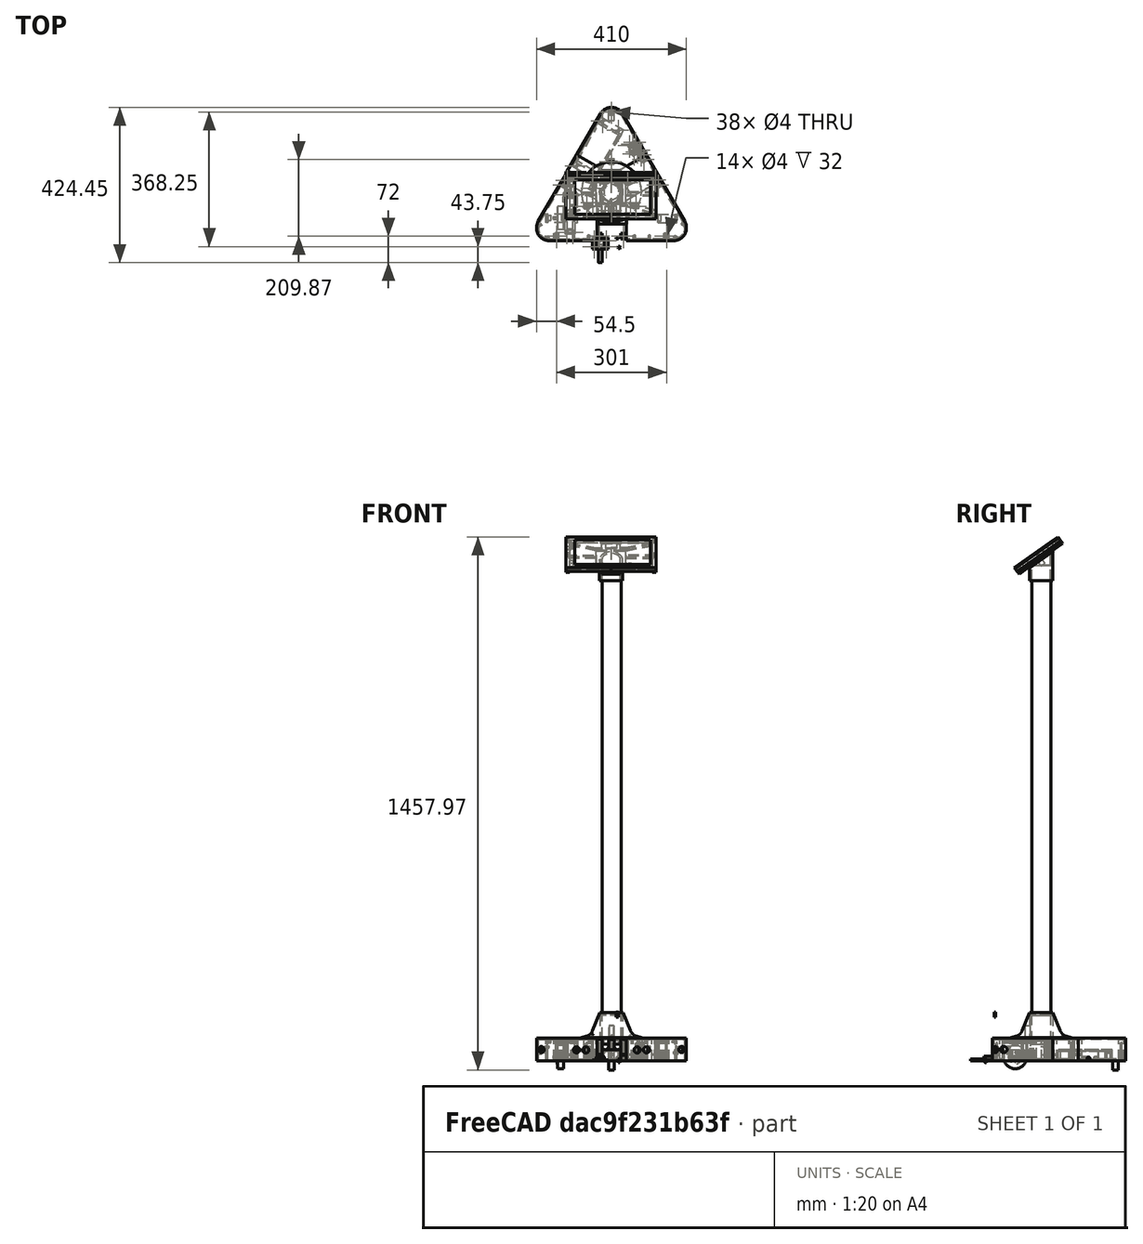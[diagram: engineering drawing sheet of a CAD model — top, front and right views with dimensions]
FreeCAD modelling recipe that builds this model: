
FCSTD DOCUMENT  (FreeCAD 0.16R6703 (Git))
Label: tabbot
License: All rights reserved
LicenseURL: http://en.wikipedia.org/wiki/All_rights_reserved
objects: Part::MultiFuse×71, Part::Cylinder×70, Part::Box×59, Part::Cut×54, Sketcher::SketchObject×18, Part::Extrusion×18, Part::Mirroring×11, App::DocumentObjectGroup×9, Part::FeaturePython×5, PartDesign::Pad×2, Part::Revolution×2, Part::Part2DObjectPython×2, Mesh::Feature×1, Image::ImagePlane×1, Part::Cone×1
note: 315 computed .brp shape members not serialized (recipe doc carries the construction recipe); baked Part::Feature solids carry a one-line shape summary decoded from their .brp

FEATURE [Part::Cylinder] Cylinder  label="Wheel"
  Angle = 360
  Height = 16
  Placement = pos=(136,62,10) rot=(0,1,0;1.5708rad)
  Radius = 31.5
FEATURE [Part::Box] Box006  label="Caster wheel"
  Height = 25
  Length = 15
  Placement = pos=(-3,329,-25) rot=(0,0,1;0rad)
  Width = 15
FEATURE [Sketcher::SketchObject] Sketch  label="Motor holder walls outline"
  sketch-geometry (17):
    g0: LineSegment StartX=20.9492 StartY=105.717 StartZ=0 EndX=5.94924 EndY=105.717 EndZ=0
    g1: LineSegment StartX=5.94924 StartY=105.717 StartZ=0 EndX=5.94924 EndY=67.2165 EndZ=0
    g2: LineSegment StartX=5.94924 StartY=67.2165 StartZ=0 EndX=78.4492 EndY=67.2165 EndZ=0
    g3: LineSegment StartX=78.4492 StartY=67.2165 StartZ=0 EndX=78.4492 EndY=73.2165 EndZ=0
    g4: LineSegment StartX=78.4492 StartY=73.2165 StartZ=0 EndX=98.4492 EndY=73.2165 EndZ=0
    g5: LineSegment StartX=98.4492 StartY=73.2165 StartZ=0 EndX=98.4492 EndY=99.7165 EndZ=0
    g6: LineSegment StartX=98.4492 StartY=99.7165 StartZ=0 EndX=93.4492 EndY=99.7165 EndZ=0
    g7: LineSegment StartX=93.4492 StartY=99.7165 StartZ=0 EndX=73.4492 EndY=99.7165 EndZ=0
    g8: LineSegment StartX=73.4492 StartY=99.7165 StartZ=0 EndX=73.4492 EndY=94.7165 EndZ=0
    g9: LineSegment StartX=73.4492 StartY=94.7165 StartZ=0 EndX=93.4492 EndY=94.7165 EndZ=0
    g10: LineSegment StartX=93.4492 StartY=94.7165 StartZ=0 EndX=93.4492 EndY=78.2165 EndZ=0
    g11: LineSegment StartX=93.4492 StartY=78.2165 StartZ=0 EndX=73.4492 EndY=78.2165 EndZ=0
    g12: LineSegment StartX=73.4492 StartY=78.2165 StartZ=0 EndX=73.4492 EndY=72.2165 EndZ=0
    g13: LineSegment StartX=73.4492 StartY=72.2165 StartZ=0 EndX=10.9492 EndY=72.2165 EndZ=0
    g14: LineSegment StartX=10.9492 StartY=72.2165 StartZ=0 EndX=10.9492 EndY=100.717 EndZ=0
    g15: LineSegment StartX=10.9492 StartY=100.717 StartZ=0 EndX=20.9492 EndY=100.717 EndZ=0
    g16: LineSegment StartX=20.9492 StartY=100.717 StartZ=0 EndX=20.9492 EndY=105.717 EndZ=0
  constraints (49):
    c: Horizontal(g0)
    c: Coincident(g0,g1)
    c: Coincident(g1,g2)
    c: Horizontal(g2)
    c: Coincident(g2,g3)
    c: Coincident(g3,g4)
    c: Horizontal(g4)
    c: Coincident(g4,g5)
    c: Vertical(g5)
    c: Coincident(g5,g6)
    c: Horizontal(g6)
    c: Coincident(g7,g8)
    c: Coincident(g8,g9)
    c: Horizontal(g9)
    c: Coincident(g9,g10)
    c: Coincident(g10,g11)
    c: Horizontal(g11)
    c: Coincident(g11,g12)
    c: Coincident(g12,g13)
    c: Horizontal(g13)
    c: Coincident(g13,g14)
    c: Coincident(g14,g15)
    c: Horizontal(g15)
    c: Coincident(g15,g16)
    c: Coincident(g16,g0)
    c: Horizontal(g7)
    c: Vertical(g10)
    c: Vertical(g12)
    c: Vertical(g14)
    c: Vertical(g1)
    c: Vertical(g16)
    c: Vertical(g3)
    c: DistanceX(g7,g7) = 20
    c: Equal(g7,g9)
    c: Vertical(g8)
    c: DistanceX(g6,g5) = 5
    c: DistanceX(g0,g14) = 5
    c: DistanceY(g15,g0) = 5
    c: DistanceX(g1,g4) = 92.5
    c: DistanceX(g0,g0) = 15
    c: DistanceY(g1,g1) = 38.5
    c: Equal(g16,g8)
    c: DistanceY(g10,g10) = 16.5
    c: DistanceY(g14,g14) = 28.5
    c: DistanceY(g2,g5) = 32.5
    c: Equal(g7,g11)
    c: Equal(g11,g4)
    c: Equal(g12,g3)
    c: Coincident(g6,g7)
FEATURE [Part::Extrusion] Extrude  label="Motor holder walls"
  Base = -> Sketch
  Dir = (0,0,49)
  Solid = true
FEATURE [PartDesign::Pad] Pad002
  Length = 3
  Length2 = 100
  Type = 0
FEATURE [Part::Cylinder] Cylinder006
  Angle = 360
  Height = 10
  Placement = pos=(1.75,3,0) rot=(0,0,1;0rad)
  Radius = 2
FEATURE [Part::MultiFuse] Fusion008  label="agujero-tornillo003"
  Placement = pos=(-8,3,5) rot=(0,1,0;3.14159rad)
  Shapes = -> [Cylinder006,Pad002]
FEATURE [Part::MultiFuse] Fusion009  label="agujero-tornillo004"
  Placement = pos=(-8,19,5) rot=(0,1,0;3.14159rad)
  Shapes = -> [Cylinder006,Pad002]
FEATURE [Part::Box] Box013  label="Screws base big"
  Height = 5
  Length = 10
  Placement = pos=(-4,67,0) rot=(0,0,1;0rad)
  Width = 38.5
FEATURE [Part::Box] Box014  label="Screws base small"
  Height = 5
  Length = 10
  Placement = pos=(98.45,73,0) rot=(0,0,1;0rad)
  Width = 26.5
FEATURE [Part::MultiFuse] Fusion011  label="Motor holder walls and wings"
  Shapes = -> [Box014,Box013,Extrude]
FEATURE [Part::MultiFuse] Fusion012  label="Screws holes small"
  Placement = pos=(113,72.5,0) rot=(0,0,1;0rad)
  Shapes = -> [Fusion009,Fusion008]
FEATURE [Part::MultiFuse] Fusion015  label="Screws holes big  "
  Placement = pos=(10.5,72.5,0) rot=(0,0,1;0rad)
FEATURE [Part::MultiFuse] Fusion016  label="Screw holes"
  Shapes = -> [Fusion012,Fusion015]
FEATURE [Sketcher::SketchObject] Sketch005  label="Motor holder ceiling outline"
  sketch-geometry (8):
    g0: LineSegment StartX=21.6465 StartY=105.635 StartZ=0 EndX=6.64649 EndY=105.635 EndZ=0
    g1: LineSegment StartX=6.64649 StartY=105.635 StartZ=0 EndX=6.64649 EndY=67.1353 EndZ=0
    g2: LineSegment StartX=6.64649 StartY=67.1353 StartZ=0 EndX=79.1465 EndY=67.1353 EndZ=0
    g3: LineSegment StartX=79.1465 StartY=67.1353 StartZ=0 EndX=79.1465 EndY=73.1353 EndZ=0
    g4: LineSegment StartX=79.1465 StartY=73.1353 StartZ=0 EndX=99.1465 EndY=73.1353 EndZ=0
    g5: LineSegment StartX=99.1465 StartY=73.1353 StartZ=0 EndX=99.1465 EndY=99.6353 EndZ=0
    g6: LineSegment StartX=99.1465 StartY=99.6353 StartZ=0 EndX=21.6465 EndY=99.6353 EndZ=0
    g7: LineSegment StartX=21.6465 StartY=99.6353 StartZ=0 EndX=21.6465 EndY=105.635 EndZ=0
  constraints (23):
    c: Horizontal(g0)
    c: Coincident(g0,g1)
    c: Coincident(g1,g2)
    c: Horizontal(g2)
    c: Coincident(g2,g3)
    c: Coincident(g3,g4)
    c: Horizontal(g4)
    c: Coincident(g4,g5)
    c: Vertical(g5)
    c: Coincident(g7,g0)
    c: Horizontal(g6)
    c: Vertical(g1)
    c: Vertical(g7)
    c: Vertical(g3)
    c: DistanceY(g7,g0) = 6
    c: DistanceX(g1,g4) = 92.5
    c: DistanceX(g0,g0) = 15
    c: DistanceY(g1,g1) = 38.5
    c: DistanceY(g2,g5) = 32.5
    c: DistanceX(g4,g4) = 20
    c: Coincident(g6,g7)
    c: DistanceY(g3,g3) = 6
    c: Coincident(g6,g5)
FEATURE [Part::Extrusion] Extrude001  label="Motor holder ceiling"
  Base = -> Sketch005
  Dir = (0,0,5)
  Placement = pos=(-0.685987,0.133377,49.0053) rot=(0,0,1;0rad)
  Solid = true
FEATURE [Part::MultiFuse] Fusion017  label="Motor holder without holes"
  Shapes = -> [Fusion011,Extrude001]
FEATURE [Part::Cylinder] Cylinder007  label="Spring hole"
  Angle = 360
  Height = 3
  Placement = pos=(52,14,-56.2) rot=(0,1,0;1.5708rad)
  Radius = 3.5
FEATURE [Part::Cylinder] Cylinder008  label="Cables hole"
  Angle = 360
  Height = 30
  Placement = pos=(3,14,-14) rot=(0,0,1;0rad)
  Radius = 5
FEATURE [Part::MultiFuse] Fusion018  label="Cable and spring holes"
  Placement = pos=(8.8,72.4,-5) rot=(0,-1,0;1.5708rad)
  Shapes = -> [Cylinder007,Cylinder008]
FEATURE [Part::MultiFuse] Fusion019  label="Holes"
  Shapes = -> [Fusion016,Fusion018]
FEATURE [Part::Cut] Cut006  label="Motor holder"
  Base = -> Fusion017
  Placement = pos=(32,126,0) rot=(0,0,-1;1.5708rad)
  Tool = -> Fusion019
FEATURE [Sketcher::SketchObject] Sketch004  label="Base Outline Bumpers"
  sketch-geometry (12):
    g0: LineSegment StartX=175 StartY=0 StartZ=0 EndX=10 EndY=0 EndZ=0
    g1: LineSegment StartX=-107.811 StartY=204.054 StartZ=0 EndX=-25.3109 EndY=346.949 EndZ=0
    g2: LineSegment StartX=35.3109 StartY=346.949 StartZ=0 EndX=117.811 EndY=204.054 EndZ=0
    g3: LineSegment StartX=-112.811 StartY=195.394 StartZ=0 EndX=-195.311 EndY=52.5 EndZ=0
    g4: LineSegment StartX=-165 StartY=0 StartZ=0 EndX=0 EndY=0 EndZ=0
    g5: LineSegment StartX=205.311 StartY=52.5 StartZ=0 EndX=122.811 EndY=195.394 EndZ=0
    g6: ArcOfCircle CenterX=-165 CenterY=35 CenterZ=0 NormalX=0 NormalY=0 NormalZ=1 Radius=35 StartAngle=2.61799 EndAngle=4.71239
    g7: ArcOfCircle CenterX=5 CenterY=329.449 CenterZ=0 NormalX=0 NormalY=0 NormalZ=1 Radius=35 StartAngle=0.523599 EndAngle=2.61799
    g8: ArcOfCircle CenterX=175 CenterY=35 CenterZ=0 NormalX=0 NormalY=0 NormalZ=1 Radius=35 StartAngle=4.71239 EndAngle=6.80678
    g9: LineSegment StartX=0 StartY=0 StartZ=0 EndX=10 EndY=0 EndZ=0
    g10: LineSegment StartX=-107.811 StartY=204.054 StartZ=0 EndX=-112.811 EndY=195.394 EndZ=0
    g11: LineSegment StartX=117.811 StartY=204.054 StartZ=0 EndX=122.811 EndY=195.394 EndZ=0
  constraints (33):
    c: Horizontal(g0)
    c: Horizontal(g4)
    c: Distance(g3,g1) = 10
    c: Parallel(g3,g1)
    c: Parallel(g2,g5)
    c: Tangent(g3,g6) = -1.5708
    c: Tangent(g4,g6) = -1.5708
    c: Tangent(g1,g7) = 1.5708
    c: Tangent(g2,g7) = 1.5708
    c: Tangent(g5,g8) = -1.5708
    c: Radius(g6) = 35
    c: Equal(g6,g7)
    c: Equal(g7,g8)
    c: Distance(g3) = 165
    c: Equal(g3,g1)
    c: Equal(g1,g2)
    c: Equal(g2,g5)
    c: Equal(g5,g0)
    c: Equal(g0,g4)
    c: Coincident(g9,g4)
    c: Coincident(g9,g0)
    c: Coincident(g0,g8)
    c: Horizontal(g9)
    c: Coincident(g10,g1)
    c: Coincident(g10,g3)
    c: Coincident(g11,g2)
    c: Coincident(g11,g5)
    c: Parallel(g10,g1)
    c: Parallel(g2,g11)
    c: Equal(g10,g11)
    c: Equal(g11,g9)
    c: Coincident(g4,g-1)
    c: Angle(g6) = 2.0944
FEATURE [Part::MultiFuse] Fusion033  label="Slider"
FEATURE [Sketcher::SketchObject] Sketch015
  Placement = pos=(0,0,0) rot=(0.57735,0.57735,0.57735;2.0944rad)
  sketch-geometry (6):
    g0: LineSegment StartX=18.75 StartY=0 StartZ=0 EndX=18.75 EndY=2 EndZ=0
    g1: LineSegment StartX=18.75 StartY=2 StartZ=0 EndX=3.75 EndY=2 EndZ=0
    g2: LineSegment StartX=18.75 StartY=0 StartZ=0 EndX=3 EndY=0 EndZ=0
    g3: LineSegment StartX=3.75 StartY=2 StartZ=0 EndX=1.5 EndY=2 EndZ=0
    g4: LineSegment StartX=1.5 StartY=2 StartZ=0 EndX=1.5 EndY=0 EndZ=0
    g5: LineSegment StartX=1.5 StartY=0 StartZ=0 EndX=3 EndY=0 EndZ=0
  constraints (18):
    c: Vertical(g0)
    c: Coincident(g0,g1)
    c: Horizontal(g1)
    c: Horizontal(g2)
    c: Coincident(g2,g0)
    c: DistanceX(g2,g2) = 15.75
    c: DistanceY(g0,g0) = 2
    c: Horizontal(g3)
    c: Coincident(g3,g4)
    c: Coincident(g4,g5)
    c: Coincident(g5,g2)
    c: Horizontal(g5)
    c: Vertical(g4)
    c: Equal(g0,g4)
    c: DistanceX(g5,g5) = 1.5
    c: DistanceX(g-1,g4) = 1.5
    c: DistanceY(g4,g-1) = 0
    c: Coincident(g3,g1)
FEATURE [Part::Revolution] Revolve
  Angle = 360
  Axis = (0,0,1)
  Base = (0,0,0)
  Solid = true
  Source = -> Sketch015
FEATURE [Sketcher::SketchObject] Sketch016
  Placement = pos=(0,0,2) rot=(0,0,1;0rad)
  sketch-geometry (3):
    g0: LineSegment StartX=-1.74642 StartY=2.8 StartZ=0 EndX=-1.74642 EndY=-2.8 EndZ=0
    g1: ArcOfCircle CenterX=0 CenterY=0 CenterZ=0 NormalX=0 NormalY=0 NormalZ=1 Radius=3.3 StartAngle=4.15471 EndAngle=8.41166
    g2: Circle CenterX=0 CenterY=0 CenterZ=0 NormalX=0 NormalY=0 NormalZ=1 Radius=4.3
  constraints (8):
    c: Vertical(g0)
    c: DistanceY(g0,g0) = 5.6
    c: Coincident(g1,g0)
    c: Coincident(g1,g0)
    c: Radius(g1) = 3.3
    c: Coincident(g2,g-1)
    c: Radius(g2) = 4.3
    c: Coincident(g1,g-1)
FEATURE [Part::Extrusion] Extrude011
  Base = -> Sketch016
  Dir = (0,0,10)
  Solid = true
FEATURE [Part::Extrusion] Extrude012  label="Base"
  Base = -> Sketch004
  Dir = (0,0,-5)
  Solid = true
FEATURE [Part::MultiFuse] Fusion039  label="Encoder piece"
  Placement = pos=(175,47,10) rot=(0,1,0;1.5708rad)
  Shapes = -> [Revolve,Extrude011]
FEATURE [Mesh::Feature] User_Library_HC_SR005  label="User Library-HC-SR005"
  Placement = pos=(-141.804,49.5,15) rot=(0.774597,-0.447214,-0.447214;1.82349rad)
FEATURE [App::DocumentObjectGroup] Group  label="Trial"
FEATURE [Part::Box] Box023  label="Battery001"
  Height = 26
  Length = 115
  Width = 60
FEATURE [Part::Box] Box024  label="Board001"
  Height = 30
  Length = 80
  Placement = pos=(-31,45,0) rot=(0,0,1;0rad)
  Width = 55
FEATURE [Part::Box] Box025  label="Switch001"
  Height = 22
  Length = 12
  Placement = pos=(0,-40,0) rot=(0,0,1;0rad)
  Width = 40
FEATURE [Part::MultiFuse] Fusion045  label="Battery + switch001"
  Placement = pos=(-29.9027,319.105,0) rot=(0,0,-1;2.0944rad)
  Shapes = -> [Box025,Box023]
FEATURE [PartDesign::Pad] Pad003
  Length = 20
  Length2 = 100
  Type = 0
FEATURE [Part::Cylinder] Cylinder013
  Angle = 360
  Height = 10
  Placement = pos=(1.75,3,0) rot=(0,0,1;0rad)
  Radius = 2
FEATURE [Sketcher::SketchObject] Sketch028  label="Battery holder walls outline001"
  sketch-geometry (10):
    g0: LineSegment StartX=19.4089 StartY=-79.555 StartZ=0 EndX=19.4089 EndY=-7.55496 EndZ=0
    g1: LineSegment StartX=19.4089 StartY=-7.55496 StartZ=0 EndX=-108.591 EndY=-7.55496 EndZ=0
    g2: LineSegment StartX=-108.591 StartY=-7.55496 StartZ=0 EndX=-108.591 EndY=-79.555 EndZ=0
    g3: LineSegment StartX=-108.591 StartY=-79.555 StartZ=0 EndX=-103.591 EndY=-79.555 EndZ=0
    g4: LineSegment StartX=-103.591 StartY=-79.555 StartZ=0 EndX=-103.591 EndY=-12.555 EndZ=0
    g5: LineSegment StartX=-103.591 StartY=-12.555 StartZ=0 EndX=14.4089 EndY=-12.555 EndZ=0
    g6: LineSegment StartX=14.4089 StartY=-12.555 StartZ=0 EndX=14.4089 EndY=-74.555 EndZ=0
    g7: LineSegment StartX=14.4089 StartY=-74.555 StartZ=0 EndX=-90.5911 EndY=-74.555 EndZ=0
    g8: LineSegment StartX=-90.5911 StartY=-74.555 StartZ=0 EndX=-90.5911 EndY=-79.555 EndZ=0
    g9: LineSegment StartX=-90.5911 StartY=-79.555 StartZ=0 EndX=19.4089 EndY=-79.555 EndZ=0
  constraints (28):
    c: Vertical(g0)
    c: Coincident(g0,g1)
    c: Horizontal(g1)
    c: Coincident(g1,g2)
    c: Vertical(g2)
    c: Coincident(g2,g3)
    c: Coincident(g3,g4)
    c: Vertical(g4)
    c: Coincident(g4,g5)
    c: Horizontal(g5)
    c: Coincident(g5,g6)
    c: Vertical(g6)
    c: Coincident(g6,g7)
    c: Horizontal(g7)
    c: Coincident(g7,g8)
    c: Vertical(g8)
    c: Coincident(g8,g9)
    c: Coincident(g9,g0)
    c: Horizontal(g9)
    c: Horizontal(g3)
    c: Equal(g2,g0)
    c: DistanceX(g3,g3) = 5
    c: DistanceY(g8,g8) = 5
    c: DistanceY(g5,g0) = 5
    c: DistanceX(g6,g0) = 5
    c: DistanceX(g5,g5) = 118
    c: DistanceX(g7,g7) = 105
    c: DistanceY(g6,g6) = 62
FEATURE [Part::Extrusion] Extrude022  label="Battery holder walls001"
  Base = -> Sketch028
  Dir = (0,0,26)
  Solid = true
FEATURE [Part::MultiFuse] Fusion046  label="battery screw 005"
  Placement = pos=(-113,-22,5) rot=(0,1,0;3.14159rad)
  Shapes = -> [Cylinder013,Pad003]
FEATURE [Part::Cylinder] Cylinder014  label="Battery cables hole001"
  Angle = 360
  Height = 20
  Placement = pos=(-98,0,8.5) rot=(1,0,0;1.5708rad)
  Radius = 4.5
FEATURE [Part::Box] Box027  label="Screw plane 003"
  Height = 5
  Length = 15
  Placement = pos=(18.5,-79.5,0) rot=(0,0,1;0rad)
  Width = 72
FEATURE [Part::Box] Box028  label="Screw plane 004"
  Height = 5
  Length = 15
  Placement = pos=(-122.5,-79.5,0) rot=(0,0,1;0rad)
  Width = 72
FEATURE [Part::MultiFuse] Fusion048  label="battery screw 006"
  Placement = pos=(-113,-72,5) rot=(0,1,0;3.14159rad)
  Shapes = -> [Cylinder013,Pad003]
FEATURE [Part::MultiFuse] Fusion049  label="battery screw 007"
  Placement = pos=(28,-72,5) rot=(0,1,0;3.14159rad)
  Shapes = -> [Cylinder013,Pad003]
FEATURE [Part::MultiFuse] Fusion050  label="battery screw 008"
  Placement = pos=(28,-22,5) rot=(0,1,0;3.14159rad)
  Shapes = -> [Cylinder013,Pad003]
FEATURE [Part::MultiFuse] Fusion051  label="Battery screws001"
  Shapes = -> [Fusion046,Fusion048,Fusion049,Fusion050]
FEATURE [Part::MultiFuse] Fusion052  label="Battery holes001"
  Shapes = -> [Fusion051,Cylinder014]
FEATURE [App::DocumentObjectGroup] Group005  label="Future"
  Group = -> [Fusion033]
FEATURE [Part::FeaturePython] Point  label="Center base"  # WARN: FeaturePython — macro-defined, semantics opaque (R4)
  X = 5
  Y = 133.15
  Z = 0
FEATURE [Sketcher::SketchObject] Sketch030  label="US sensor holes 001"
  Placement = pos=(0,0,0) rot=(1,0,0;1.5708rad)
  sketch-geometry (2):
    g0: Circle CenterX=-50.6795 CenterY=14.9384 CenterZ=0 NormalX=0 NormalY=0 NormalZ=1 Radius=8.5
    g1: Circle CenterX=-25.1765 CenterY=14.826 CenterZ=0 NormalX=0 NormalY=0 NormalZ=1 Radius=8.5
  constraints (2):
    c: Radius(g0) = 8.5
    c: Equal(g0,g1) = 9
FEATURE [Part::Extrusion] Extrude027  label="US holes003"
  Base = -> Sketch030
  Dir = (0,50,0)
  Placement = pos=(0,-11,15) rot=(0,0,1;0rad)
  Solid = true
FEATURE [Part::Extrusion] Extrude028  label="US holes004"
  Base = -> Sketch030
  Dir = (0,50,0)
  Placement = pos=(-145,-20,16) rot=(0,0,-1;1.0472rad)
  Solid = true
FEATURE [Sketcher::SketchObject] Sketch031  label="US sensor holes screws001"
  Placement = pos=(0,0,0) rot=(1,0,0;1.5708rad)
  sketch-geometry (2):
    g0: Circle CenterX=-57.9482 CenterY=6.7605 CenterZ=0 NormalX=0 NormalY=0 NormalZ=1 Radius=1.4
    g1: Circle CenterX=-17.0367 CenterY=23.1516 CenterZ=0 NormalX=0 NormalY=0 NormalZ=1 Radius=1.4
  constraints (2):
    c: Radius(g0) = 1.4
    c: Equal(g0,g1) = 1.4
FEATURE [Part::Extrusion] Extrude029  label="US sensor holes screws extruded001"
  Base = -> Sketch031
  Dir = (0,30,0)
  Placement = pos=(0,5,15) rot=(0,0,1;0rad)
  Solid = true
FEATURE [Part::MultiFuse] Fusion057  label="US holes005"
  Placement = pos=(-40,0,0) rot=(0,0,1;0rad)
  Shapes = -> [Extrude027,Extrude028]
FEATURE [Part::Box] Box029  label="Wall 003"
  Height = 58
  Length = 130
  Placement = pos=(-125,0,0) rot=(0,0,1;0rad)
  Width = 5
FEATURE [Part::Cylinder] Cylinder015  label="Curve out001"
  Angle = 120
  Height = 58
  Placement = pos=(-100,35,0) rot=(0,0,1;2.61799rad)
  Radius = 35
FEATURE [Part::Box] Box030  label="Wall 004"
  Height = 58
  Length = 130
  Placement = pos=(-150.981,50,0) rot=(0,0,1;1.0472rad)
  Width = 5
FEATURE [Part::Cylinder] Cylinder016  label="Curve in001"
  Angle = 120
  Height = 58
  Placement = pos=(-100,35,0) rot=(0,0,1;2.61799rad)
  Radius = 30
FEATURE [Part::Cut] Cut020  label="Curve001"
  Base = -> Cylinder015
  Placement = pos=(-25,0,0) rot=(0,0,1;0rad)
  Tool = -> Cylinder016
FEATURE [Part::Box] Box031  label="Top 002"
  Height = 4
  Length = 130
  Placement = pos=(-125,0,58) rot=(0,0,1;0rad)
  Width = 35
FEATURE [Part::Cylinder] Cylinder017  label="Top curve001"
  Angle = 120
  Height = 4
  Placement = pos=(-125,35,58) rot=(0,0,1;2.61799rad)
  Radius = 35
FEATURE [Part::MultiFuse] Fusion058  label="Bumper walls"
  Placement = pos=(-40,0,0) rot=(0,0,1;0rad)
  Shapes = -> [Box029,Box030,Cut020]
FEATURE [Part::Box] Box032  label="Support 004"
  Height = 6
  Length = 6
  Placement = pos=(-20,5,35) rot=(0,0,1;0rad)
  Width = 10
FEATURE [Part::Box] Box033  label="Support 005"
  Height = 6
  Length = 6
  Placement = pos=(-61,5,19) rot=(0,0,1;0rad)
  Width = 10
FEATURE [Part::MultiFuse] Fusion059  label="Support 006"
  Shapes = -> [Box032,Box033]
FEATURE [Part::Cut] Cut024  label="US support003"
  Base = -> Fusion059
  Placement = pos=(-40,0,0) rot=(0,0,1;0rad)
  Tool = -> Extrude029
FEATURE [Part::Cut] Cut025  label="US support004"
  Base = -> Fusion059
  Placement = pos=(-171,-13,0) rot=(0,0,-1;1.0472rad)
  Tool = -> Extrude029
FEATURE [Part::Box] Box034  label="Top 003"
  Height = 4
  Length = 130
  Placement = pos=(-90.3109,165.083,58) rot=(0,0,-1;2.0944rad)
  Width = 35
FEATURE [Part::MultiFuse] Fusion066  label="Bumper walls001"
  Placement = pos=(-87.811,238.695,0) rot=(0,0,-1;2.0944rad)
  Shapes = -> [Box029,Box030,Cut020]
FEATURE [Part::Box] Box  label="Cube"
  Height = 58
  Length = 15
  Placement = pos=(-13,5,0) rot=(0,0,1;0rad)
  Width = 15
FEATURE [Part::Cylinder] Cylinder018  label="Cylinder"
  Angle = 360
  Height = 50
  Placement = pos=(-5.5,12,0) rot=(0,0,1;0rad)
  Radius = 2
FEATURE [Part::Cut] Cut  label="Bumper support 001"
  Base = -> Box
  Tool = -> Cylinder018
FEATURE [Part::Box] Box035  label="Nut hole"
  Height = 3
  Length = 6
  Placement = pos=(-8.5,5,15) rot=(0,0,1;0rad)
  Width = 15
FEATURE [Part::Cut] Cut031  label="Bumper support 005"
  Base = -> Cut
  Placement = pos=(-140,0,0) rot=(0,0,1;0rad)
  Tool = -> Box035
FEATURE [Part::Cut] Cut032  label="Bumper support 006"
  Base = -> Cut
  Placement = pos=(-136.811,153.825,0) rot=(0,0,-1;2.0944rad)
  Tool = -> Box035
FEATURE [Sketcher::SketchObject] Sketch032
  Placement = pos=(0,0,0) rot=(1,0,0;1.5708rad)
  sketch-geometry (7):
    g0: LineSegment StartX=12.1868 StartY=134.984 StartZ=0 EndX=32.1868 EndY=134.984 EndZ=0
    g1: LineSegment StartX=32.1868 StartY=134.984 StartZ=0 EndX=52.1868 EndY=84.9837 EndZ=0
    g2: LineSegment StartX=69.6638 StartY=69.9351 StartZ=0 EndX=82.1868 EndY=66.9837 EndZ=0
    g3: LineSegment StartX=82.1868 StartY=66.9837 StartZ=0 EndX=82.1868 EndY=64.9837 EndZ=0
    g4: LineSegment StartX=82.1868 StartY=64.9837 StartZ=0 EndX=12.1868 EndY=64.9837 EndZ=0
    g5: ArcOfCircle CenterX=75.3987 CenterY=94.2684 CenterZ=0 NormalX=0 NormalY=0 NormalZ=1 Radius=25 StartAngle=3.5221 EndAngle=4.48093
    g6: LineSegment StartX=12.1868 StartY=64.9837 StartZ=0 EndX=12.1868 EndY=134.984 EndZ=0
  constraints (18):
    c: Horizontal(g0)
    c: Coincident(g0,g1)
    c: Coincident(g2,g3)
    c: Coincident(g3,g4)
    c: Horizontal(g4)
    c: Vertical(g3)
    c: DistanceY(g3,g3) = 2
    c: Tangent(g1,g5) = -1.5708
    c: Tangent(g2,g5) = -1.5708
    c: DistanceX(g0,g0) = 20
    c: DistanceY(g3,g0) = 70
    c: DistanceX(g0,g2) = 50
    c: DistanceY(g1,g1) = 50
    c: DistanceX(g1,g1) = 20
    c: Coincident(g4,g6)
    c: Coincident(g6,g0)
    c: Vertical(g6)
    c: Radius(g5) = 25
FEATURE [Part::Revolution] Revolve001  label="Embellecedor"
  Angle = 360
  Axis = (0,0,1)
  Base = (0,0,0)
  Placement = pos=(5,133,0) rot=(0,0,1;0rad)
  Solid = true
  Source = -> Sketch032
FEATURE [Part::MultiFuse] Fusion075  label="Tubes"
FEATURE [Part::Part2DObjectPython] DWire  # Draft 2D object (typed FeaturePython)
  ChamferSize = 0
  Closed = true
  End = (5,110.056,62)
  FilletRadius = 0
  Length = 410.111
  MakeFace = true
  Points = (4) [(-60,147.583,62),(-125,35,62),(5,35,62),(5,110.056,62)]
  Start = (-60,147.583,62)
  Subdivisions = 0
FEATURE [Part::Extrusion] Extrude030
  Base = -> DWire
  Dir = (0,0,-4)
  Solid = true
FEATURE [Part::MultiFuse] Fusion076  label="Bumper top"
  Placement = pos=(-40,0,0) rot=(0,0,1;0rad)
  Shapes = -> [Cylinder017,Box034,Box031,Extrude030]
FEATURE [Part::Box] Box038  label="Cube002"
  Height = 58
  Length = 80
  Placement = pos=(-35,0,0) rot=(0,0,1;0rad)
  Width = 5
FEATURE [Part::Box] Box039  label="Cube003"
  Height = 4
  Length = 80
  Placement = pos=(-35,0,58) rot=(0,0,1;0rad)
  Width = 90
FEATURE [Part::MultiFuse] Fusion081  label="Extension 001"
  Shapes = -> [Box039,Box038]
FEATURE [Part::Cut] Cut037  label="Bumper support 011"
  Base = -> Cut
  Placement = pos=(-22,0,0) rot=(0,0,1;0rad)
  Tool = -> Box035
FEATURE [Part::Cut] Cut038  label="Bumper support 012"
  Base = -> Cut
  Placement = pos=(43,0,0) rot=(0,0,1;0rad)
  Tool = -> Box035
FEATURE [Part::Cut] Cut039  label="Bumper support 013"
  Base = -> Cut
  Placement = pos=(10,70,0) rot=(0,0,1;0rad)
  Tool = -> Box035
FEATURE [Part::MultiFuse] Fusion082  label="Extension supports"
  Shapes = -> [Cut039,Cut037,Cut038]
FEATURE [Part::MultiFuse] Fusion083  label="M3 screw"
  Placement = pos=(28,-22,5) rot=(0,1,0;3.14159rad)
  Shapes = -> [Cylinder013,Pad003]
FEATURE [Part::Cylinder] Cylinder021  label="M3 hole"
  Angle = 360
  Height = 15
  Placement = pos=(-46.5,104,58) rot=(0,0,1;0rad)
  Radius = 2
FEATURE [Part::Cylinder] Cylinder022  label="M3 hole001"
  Angle = 360
  Height = 15
  Placement = pos=(-46.5,104,58) rot=(0,0,1;0rad)
  Radius = 2
FEATURE [Part::Cut] Cut041  label="Bumper top with hole"
  Base = -> Fusion076
  Tool = -> Cylinder021
FEATURE [Part::MultiFuse] Fusion084  label="Extension with supports 001"
  Shapes = -> [Fusion081,Fusion082]
FEATURE [Part::FeaturePython] Clone002  label="Extension with supports 002"  # Draft clone (typed FeaturePython)
  Objects = -> [Fusion084]
  Placement = pos=(122.811,195.394,0) rot=(0,0,1;2.0944rad)
  Scale = (1,1,1)
FEATURE [Part::FeaturePython] Clone004  label="Clone of Bumper top with hole"  # Draft clone (typed FeaturePython)
  Objects = -> [Cut041]
  Placement = pos=(-107.811,204.054,0) rot=(0,0,-1;2.0944rad)
  Scale = (1,1,1)
FEATURE [Part::Cut] Cut042  label="Bumper support 014"
  Base = -> Cut
  Placement = pos=(-57,82,0) rot=(0,0,1;0rad)
  Tool = -> Box035
FEATURE [Part::MultiFuse] Fusion085  label="Bumper supports"
  Shapes = -> [Cut031,Cut042,Cut032]
FEATURE [Part::Box] Box040  label="Cube004"
  Height = 58
  Length = 15
  Placement = pos=(-13,5,0) rot=(0,0,1;0rad)
  Width = 15
FEATURE [Part::Cylinder] Cylinder023  label="Cylinder015"
  Angle = 360
  Height = 50
  Placement = pos=(-5.5,12,0) rot=(0,0,1;0rad)
  Radius = 2
FEATURE [Part::Cut] Cut043  label="Bumper support 015"
  Base = -> Box040
  Tool = -> Cylinder023
FEATURE [Part::Box] Box041  label="Nut hole001"
  Height = 4
  Length = 8
  Placement = pos=(-9.5,5,15) rot=(0,0,1;0rad)
  Width = 15
FEATURE [Part::Cut] Cut044  label="Bumper support 016"
  Base = -> Cut043
  Placement = pos=(10,340,0) rot=(0,0,1;0rad)
  Tool = -> Box041
FEATURE [Part::Cut] Cut045  label="Bumper support 017"
  Base = -> Cut043
  Placement = pos=(10,204,0) rot=(0,0,1;0rad)
  Tool = -> Box041
FEATURE [Part::Cut] Cut046  label="Bumper support 018"
  Base = -> Cut043
  Placement = pos=(93.7959,245.482,0) rot=(0,0,1;2.0944rad)
  Tool = -> Box041
FEATURE [Part::MultiFuse] Fusion088  label="Supports bumper back "
  Shapes = -> [Cut044,Cut046,Cut045]
FEATURE [Part::MultiFuse] Fusion089  label="Bumper back"
  Shapes = -> [Clone004,Fusion066,Fusion088]
FEATURE [Part::Box] Box042  label="Cube005"
  Height = 58
  Length = 15
  Placement = pos=(-13,5,0) rot=(0,0,1;0rad)
  Width = 15
FEATURE [Part::Cylinder] Cylinder024  label="Cylinder016"
  Angle = 360
  Height = 50
  Placement = pos=(-5.5,12,0) rot=(0,0,1;0rad)
  Radius = 2
FEATURE [Part::Cut] Cut047  label="Bumper support 019"
  Base = -> Box042
  Tool = -> Cylinder024
FEATURE [Part::Box] Box043  label="Nut hole002"
  Height = 3
  Length = 6
  Placement = pos=(-8.5,5,15) rot=(0,0,1;0rad)
  Width = 15
FEATURE [Part::Box] Box044  label="Cube006"
  Height = 58
  Length = 80
  Placement = pos=(-35,0,0) rot=(0,0,1;0rad)
  Width = 5
FEATURE [Part::Box] Box045  label="Cube007"
  Height = 4
  Length = 80
  Placement = pos=(-35,0,58) rot=(0,0,1;0rad)
  Width = 90
FEATURE [Part::MultiFuse] Fusion090  label="Extension 002"
  Placement = pos=(-107.811,204.054,0) rot=(0,0,-1;2.0944rad)
  Shapes = -> [Box045,Box044]
FEATURE [Part::Cut] Cut049  label="Bumper support 021"
  Base = -> Cut047
  Placement = pos=(43,0,0) rot=(0,0,1;0rad)
  Tool = -> Box043
FEATURE [Part::Cut] Cut050  label="Bumper support 022"
  Base = -> Cut047
  Placement = pos=(10,70,0) rot=(0,0,1;0rad)
  Tool = -> Box043
FEATURE [Part::Cut] Cut048  label="Bumper support 020"
  Base = -> Cut047
  Placement = pos=(-22,0,0) rot=(0,0,1;0rad)
  Tool = -> Box043
FEATURE [Part::MultiFuse] Fusion091  label="Extension supports001"
  Shapes = -> [Cut050,Cut048,Cut049]
FEATURE [Part::Cut] Cut051  label="Bumper support 023"
  Base = -> Cut
  Placement = pos=(-102.16,163.842,0) rot=(0,0,1;1.0472rad)
  Tool = -> Box035
FEATURE [Part::Cut] Cut052  label="Bumper support 024"
  Base = -> Cut
  Placement = pos=(-33.7717,142.497,0) rot=(0,0,1;1.0472rad)
  Tool = -> Box035
FEATURE [Part::MultiFuse] Fusion092  label="Extension with supports 003"
  Shapes = -> [Fusion090,Cut051,Cut052]
FEATURE [App::DocumentObjectGroup] Group006  label="Extensions"
  Group = -> [Fusion084,Clone002,Fusion092]
FEATURE [Part::Cylinder] Cylinder025  label="M3 hole002"
  Angle = 360
  Height = 15
  Placement = pos=(-46.5,104,58) rot=(0,0,1;0rad)
  Radius = 2
FEATURE [Part::Cylinder] Cylinder026  label="M3 hole003"
  Angle = 360
  Height = 15
  Placement = pos=(56.5,104,58) rot=(0,0,1;0rad)
  Radius = 2
FEATURE [Part::Cylinder] Cylinder027  label="M3 hole004"
  Angle = 360
  Height = 15
  Placement = pos=(5.5,192.5,58) rot=(0,0,1;0rad)
  Radius = 2
FEATURE [Part::Box] Box046  label="Cube008"
  Height = 5
  Length = 52
  Placement = pos=(154.769,38,49.0053) rot=(0,0,1;0rad)
  Width = 23
FEATURE [Part::Box] Box047  label="Cube009"
  Height = 49
  Length = 5
  Placement = pos=(201.769,38,0.00526065) rot=(0,0,1;0rad)
  Width = 23
FEATURE [Part::MultiFuse] Fusion094  label="Encoder support"
  Placement = pos=(0,-4,0) rot=(0,0,1;0rad)
  Shapes = -> [Box046,Box047]
FEATURE [Part::Box] Box048  label="Cube010"
  Height = 40
  Length = 2
  Placement = pos=(203.5,37,2) rot=(0,0,1;0rad)
  Width = 19
FEATURE [Part::Cylinder] Cylinder030  label="M3 hole007"
  Angle = 360
  Height = 15
  Placement = pos=(163.5,47,22.5) rot=(0,1,0;1.5708rad)
  Radius = 1.5
FEATURE [Part::Cylinder] Cylinder031  label="M3 hole008"
  Angle = 360
  Height = 15
  Placement = pos=(163.5,47,-2.5) rot=(0,1,0;1.5708rad)
  Radius = 1.5
FEATURE [Part::MultiFuse] Fusion096  label="Encoder-to-wheel holes"
  Shapes = -> [Cylinder030,Cylinder031]
FEATURE [Part::Cut] Cut055  label="Encoder-to-wheel piece"
  Base = -> Fusion039
  Placement = pos=(-23,15,0) rot=(0,0,1;0rad)
  Tool = -> Fusion096
FEATURE [Part::MultiFuse] Fusion  label="Battery support without holes"
  Shapes = -> [Extrude022,Box027,Box028]
FEATURE [Part::Cut] Cut056  label="Battery support without ceiling"
  Base = -> Fusion
  Placement = pos=(-16.6317,192.981,0) rot=(0,0,-1;2.0944rad)
  Tool = -> Fusion052
FEATURE [Part::Box] Box049  label="Battery support top"
  Height = 5
  Length = 128
  Placement = pos=(-31.2328,326.801,26) rot=(0,0,-1;2.0944rad)
  Width = 72
FEATURE [Part::MultiFuse] Fusion097  label="Battery support"
  Shapes = -> [Cut056,Box049]
FEATURE [Part::Cut] Cut040  label="Trim with pipe hole"
  Base = -> Revolve001
  Tool = -> Fusion075
FEATURE [Part::MultiFuse] Fusion098  label="Trim holes"
  Shapes = -> [Cylinder025,Cylinder026,Cylinder027]
FEATURE [Part::Cut] Cut057  label="Trim with support holes"
  Base = -> Cut040
  Tool = -> Fusion098
FEATURE [Part::Box] Box050  label="Cube011"
  Height = 50
  Length = 13
  Placement = pos=(-1.5,90,50) rot=(0,0,1;0.017453rad)
  Width = 13
FEATURE [Part::Cut] Cut058  label="Trim complete"
  Base = -> Cut057
  Placement = pos=(0,0,-3) rot=(0,0,1;0rad)
  Tool = -> Box050
FEATURE [Sketcher::SketchObject] Sketch033
  Placement = pos=(0,0,0) rot=(1,0,0;1.5708rad)
  sketch-geometry (31):
    g0: LineSegment StartX=-81.8917 StartY=135.847 StartZ=0 EndX=-71.8917 EndY=135.847 EndZ=0
    g1: LineSegment StartX=-71.8917 StartY=135.847 StartZ=0 EndX=-71.8917 EndY=125.847 EndZ=0
    g2: LineSegment StartX=-71.8917 StartY=125.847 StartZ=0 EndX=0.608279 EndY=103.681 EndZ=0
    g3: LineSegment StartX=40.6083 StartY=103.681 StartZ=0 EndX=40.6083 EndY=22.012 EndZ=0
    g4: LineSegment StartX=0.608279 StartY=22.012 StartZ=0 EndX=-71.8917 EndY=-0.153498 EndZ=0
    g5: LineSegment StartX=-71.8917 StartY=-0.153498 StartZ=0 EndX=-71.8917 EndY=-10.1535 EndZ=0
    g6: LineSegment StartX=-71.8917 StartY=-10.1535 StartZ=0 EndX=-81.8917 EndY=-10.1535 EndZ=0
    g7: LineSegment StartX=-81.8917 StartY=-10.1535 StartZ=0 EndX=-81.8917 EndY=6.7892 EndZ=0
    g8: LineSegment StartX=-81.8917 StartY=6.7892 StartZ=0 EndX=0.608279 EndY=32.012 EndZ=0
    g9: LineSegment StartX=0.608279 StartY=32.012 StartZ=0 EndX=0.608279 EndY=57.8465 EndZ=0
    g10: LineSegment StartX=0.608279 StartY=57.8465 StartZ=0 EndX=-81.8917 EndY=57.8465 EndZ=0
    g11: LineSegment StartX=-81.8917 StartY=57.8465 StartZ=0 EndX=-81.8917 EndY=67.8465 EndZ=0
    g12: LineSegment StartX=-81.8917 StartY=67.8465 StartZ=0 EndX=0.608279 EndY=67.8465 EndZ=0
    g13: LineSegment StartX=0.608279 StartY=67.8465 StartZ=0 EndX=0.608279 EndY=93.681 EndZ=0
    g14: LineSegment StartX=0.608279 StartY=93.681 StartZ=0 EndX=-81.8917 EndY=118.904 EndZ=0
    g15: LineSegment StartX=-81.8917 StartY=118.904 StartZ=0 EndX=-81.8917 EndY=135.847 EndZ=0
    g16: Circle CenterX=-76.8917 CenterY=130.847 CenterZ=0 NormalX=0 NormalY=0 NormalZ=1 Radius=2
    g17: Circle CenterX=-76.8917 CenterY=62.8465 CenterZ=0 NormalX=0 NormalY=0 NormalZ=1 Radius=2
    g18: Circle CenterX=-76.8917 CenterY=-5.1535 CenterZ=0 NormalX=0 NormalY=0 NormalZ=1 Radius=2
    g19: LineSegment StartX=0.608279 StartY=103.681 StartZ=0 EndX=15.6083 EndY=103.681 EndZ=0
    g20: LineSegment StartX=15.6083 StartY=103.681 StartZ=0 EndX=15.6083 EndY=135.681 EndZ=0
    g21: LineSegment StartX=15.6083 StartY=135.681 StartZ=0 EndX=25.6083 EndY=135.681 EndZ=0
    g22: LineSegment StartX=25.6083 StartY=135.681 StartZ=0 EndX=25.6083 EndY=103.681 EndZ=0
    g23: LineSegment StartX=25.6083 StartY=103.681 StartZ=0 EndX=40.6083 EndY=103.681 EndZ=0
    g24: LineSegment StartX=0.608279 StartY=22.012 StartZ=0 EndX=15.6083 EndY=22.012 EndZ=0
    g25: LineSegment StartX=15.6083 StartY=22.012 StartZ=0 EndX=15.6083 EndY=-9.98802 EndZ=0
    g26: LineSegment StartX=15.6083 StartY=-9.98802 StartZ=0 EndX=25.6083 EndY=-9.98802 EndZ=0
    g27: LineSegment StartX=25.6083 StartY=-9.98802 StartZ=0 EndX=25.6083 EndY=22.012 EndZ=0
    g28: LineSegment StartX=25.6083 StartY=22.012 StartZ=0 EndX=40.6083 EndY=22.012 EndZ=0
    g29: Circle CenterX=20.6083 CenterY=130.681 CenterZ=0 NormalX=0 NormalY=0 NormalZ=1 Radius=2
    g30: Circle CenterX=20.6083 CenterY=-4.98802 CenterZ=0 NormalX=0 NormalY=0 NormalZ=1 Radius=2
  constraints (91):
    c: Horizontal(g0)
    c: Coincident(g0,g1)
    c: Vertical(g1)
    c: Coincident(g1,g2)
    c: Vertical(g3)
    c: Coincident(g4,g5)
    c: Vertical(g5)
    c: Coincident(g5,g6)
    c: Horizontal(g6)
    c: Coincident(g6,g7)
    c: Vertical(g7)
    c: Coincident(g7,g8)
    c: Coincident(g8,g9)
    c: Vertical(g9)
    c: Coincident(g9,g10)
    c: Horizontal(g10)
    c: Coincident(g10,g11)
    c: Coincident(g11,g12)
    c: Horizontal(g12)
    c: Coincident(g12,g13)
    c: Coincident(g13,g14)
    c: Coincident(g14,g15)
    c: Coincident(g15,g0)
    c: Vertical(g13)
    c: Vertical(g11)
    c: Radius(g16) = 2
    c: DistanceX(g0,g16) = 5
    c: DistanceY(g16,g0) = 5
    c: Vertical(g15)
    c: DistanceX(g0,g0) = 10
    c: DistanceX(g1,g3) = 112.5
    c: Equal(g16,g17)
    c: Equal(g17,g18)
    c: Parallel(g14,g2)
    c: Parallel(g4,g8)
    c: DistanceX(g6,g18) = 5
    c: DistanceY(g6,g18) = 5
    c: DistanceX(g6,g6) = 10
    c: DistanceY(g5,g5) = 10
    c: DistanceY(g1,g1) = 10
    c: DistanceX(g11,g17) = 5
    c: DistanceY(g17,g11) = 5
    c: DistanceY(g11,g11) = 10
    c: DistanceX(g11,g3) = 122.5
    c: DistanceX(g5,g3) = 112.5
    c: DistanceX(g2,g3) = 40
    c: DistanceX(g9,g3) = 40
    c: Distance(g13,g2) = 10
    c: DistanceX(g13,g3) = 40
    c: Distance(g8,g4) = 10
    c: DistanceX(g8,g4) = 0
    c: DistanceY(g4,g1) = 126
    c: Equal(g13,g9)
    c: Coincident(g2,g19)
    c: Horizontal(g19)
    c: Coincident(g19,g20)
    c: Vertical(g20)
    c: Coincident(g20,g21)
    c: Horizontal(g21)
    c: Coincident(g21,g22)
    c: Vertical(g22)
    c: Coincident(g22,g23)
    c: Coincident(g23,g3)
    c: Horizontal(g23)
    c: Angle(g19,g2) = 2.84489
    c: Coincident(g4,g24)
    c: Horizontal(g24)
    c: Coincident(g24,g25)
    c: Vertical(g25)
    c: Coincident(g25,g26)
    c: Horizontal(g26)
    c: Coincident(g26,g27)
    c: Vertical(g27)
    c: Coincident(g27,g28)
    c: Horizontal(g28)
    c: Coincident(g3,g28)
    c: DistanceY(g27,g27) = 32
    c: DistanceX(g26,g26) = 10
    c: Angle(g4,g24) = 2.84489
    c: DistanceX(g21,g21) = 10
    c: DistanceY(g22,g22) = 32
    c: Equal(g23,g19)
    c: Equal(g22,g20)
    c: Equal(g27,g25)
    c: Equal(g16,g29)
    c: DistanceY(g29,g20) = 5
    c: DistanceX(g20,g29) = 5
    c: DistanceY(g25,g30) = 5
    c: DistanceX(g30,g26) = 5
    c: Equal(g18,g30)
    c: Equal(g28,g24)
FEATURE [Part::Box] Box051  label="Tablet"
  Height = 126
  Length = 225
  Placement = pos=(-107.5,69.75,1352.2) rot=(-1,0,0;0.959931rad)
  Width = 9.5
FEATURE [Part::Extrusion] Extrude031
  Base = -> Sketch033
  Dir = (0,4,0)
  Placement = pos=(-0.0596972,5.44952,-7.78156) rot=(-1,0,0;0.959931rad)
  Solid = true
FEATURE [Part::Mirroring] Part__Mirroring001  label="Rear tablet holder"
  Base = (41,0,0)
  Normal = (1,0,0)
  Source = -> Extrude031
FEATURE [Sketcher::SketchObject] Sketch034
  Placement = pos=(0,0,0) rot=(1,0,0;1.5708rad)
  sketch-geometry (8):
    g0: LineSegment StartX=-82.7977 StartY=136.012 StartZ=0 EndX=-82.7977 EndY=-9.98759 EndZ=0
    g1: LineSegment StartX=-82.7977 StartY=-9.98759 StartZ=0 EndX=40.7023 EndY=-9.98759 EndZ=0
    g2: LineSegment StartX=40.7023 StartY=136.012 StartZ=0 EndX=-82.7977 EndY=136.012 EndZ=0
    g3: LineSegment StartX=-67.7977 StartY=121.012 StartZ=0 EndX=-67.7977 EndY=5.01241 EndZ=0
    g4: LineSegment StartX=-67.7977 StartY=5.01241 StartZ=0 EndX=40.7023 EndY=5.01241 EndZ=0
    g5: LineSegment StartX=40.7023 StartY=121.012 StartZ=0 EndX=-67.7977 EndY=121.012 EndZ=0
    g6: LineSegment StartX=40.7023 StartY=-9.98759 StartZ=0 EndX=40.7023 EndY=5.01241 EndZ=0
    g7: LineSegment StartX=40.7023 StartY=136.012 StartZ=0 EndX=40.7023 EndY=121.012 EndZ=0
  constraints (22):
    c: Vertical(g0)
    c: Coincident(g0,g1)
    c: Horizontal(g1)
    c: Coincident(g2,g0)
    c: Horizontal(g2)
    c: Vertical(g3)
    c: Coincident(g3,g4)
    c: Horizontal(g4)
    c: Horizontal(g5)
    c: DistanceX(g2,g2) = 123.5
    c: Equal(g1,g2)
    c: Coincident(g5,g3)
    c: Coincident(g1,g6)
    c: Vertical(g6)
    c: Coincident(g7,g2)
    c: Vertical(g7)
    c: Coincident(g7,g5)
    c: Coincident(g6,g4)
    c: DistanceY(g7,g7) = 15
    c: Equal(g7,g6)
    c: DistanceX(g0,g3) = 15
    c: DistanceY(g0,g0) = 146
FEATURE [Part::Extrusion] Extrude032  label="Upper tablet holder 001"
  Base = -> Sketch034
  Dir = (0,4,0)
  Placement = pos=(0.307074,-3.5,-0.189426) rot=(0,0,1;0rad)
  Solid = true
FEATURE [Sketcher::SketchObject] Sketch035
  Placement = pos=(0,0,0) rot=(1,0,0;1.5708rad)
  sketch-geometry (13):
    g0: LineSegment StartX=-81.0201 StartY=134.138 StartZ=0 EndX=-81.0201 EndY=-11.8622 EndZ=0
    g1: LineSegment StartX=-81.0201 StartY=-11.8622 StartZ=0 EndX=42.4799 EndY=-11.8622 EndZ=0
    g2: LineSegment StartX=42.4799 StartY=134.138 StartZ=0 EndX=-81.0201 EndY=134.138 EndZ=0
    g3: LineSegment StartX=-71.0201 StartY=124.138 StartZ=0 EndX=-71.0201 EndY=-1.86223 EndZ=0
    g4: LineSegment StartX=-71.0201 StartY=-1.86223 StartZ=0 EndX=42.4799 EndY=-1.86223 EndZ=0
    g5: LineSegment StartX=42.4799 StartY=124.138 StartZ=0 EndX=-71.0201 EndY=124.138 EndZ=0
    g6: LineSegment StartX=42.4799 StartY=-11.8622 StartZ=0 EndX=42.4799 EndY=-1.86223 EndZ=0
    g7: LineSegment StartX=42.4799 StartY=134.138 StartZ=0 EndX=42.4799 EndY=124.138 EndZ=0
    g8: Circle CenterX=-76.0201 CenterY=129.138 CenterZ=0 NormalX=0 NormalY=0 NormalZ=1 Radius=2
    g9: Circle CenterX=22.4799 CenterY=129.138 CenterZ=0 NormalX=0 NormalY=0 NormalZ=1 Radius=2
    g10: Circle CenterX=-76.0201 CenterY=61.1378 CenterZ=0 NormalX=0 NormalY=0 NormalZ=1 Radius=2
    g11: Circle CenterX=-76.0201 CenterY=-6.86223 CenterZ=0 NormalX=0 NormalY=0 NormalZ=1 Radius=2
    g12: Circle CenterX=22.4799 CenterY=-6.86223 CenterZ=0 NormalX=0 NormalY=0 NormalZ=1 Radius=2
  constraints (35):
    c: Vertical(g0)
    c: Coincident(g0,g1)
    c: Horizontal(g1)
    c: Coincident(g2,g0)
    c: Horizontal(g2)
    c: Vertical(g3)
    c: Coincident(g3,g4)
    c: Horizontal(g4)
    c: Horizontal(g5)
    c: DistanceX(g2,g2) = 123.5
    c: Equal(g1,g2)
    c: Coincident(g5,g3)
    c: Coincident(g1,g6)
    c: Vertical(g6)
    c: Coincident(g7,g2)
    c: Vertical(g7)
    c: Coincident(g7,g5)
    c: Coincident(g6,g4)
    c: DistanceY(g7,g7) = 10
    c: Equal(g7,g6)
    c: DistanceX(g0,g3) = 10
    c: DistanceY(g0,g0) = 146
    c: Radius(g8) = 2
    c: DistanceX(g0,g8) = 5
    c: DistanceY(g8,g0) = 5
    c: Equal(g8,g9) = 2
    c: DistanceX(g9,g2) = 20
    c: DistanceY(g9,g2) = 5
    c: Equal(g8,g10) = 2
    c: DistanceX(g0,g10) = 5
    c: DistanceY(g10,g0) = 73
    c: DistanceX(g0,g11) = 5
    c: DistanceY(g0,g11) = 5
    c: DistanceX(g12,g4) = 20
    c: DistanceY(g1,g12) = 5
FEATURE [Part::Extrusion] Extrude033  label="Upper tablet holder 002"
  Base = -> Sketch035
  Dir = (0,9,0)
  Placement = pos=(-0.961188,0.5,1.68521) rot=(0,0,1;0rad)
  Solid = true
FEATURE [Part::Box] Box052  label="Nut hole003"
  Height = 6
  Length = 9
  Placement = pos=(-80.5,5,59.75) rot=(0,0,1;0rad)
  Width = 3
FEATURE [Part::Box] Box053  label="Nut hole004"
  Height = 6
  Length = 15
  Placement = pos=(-81,5,130.6) rot=(0,1,0;0.785398rad)
  Width = 3
FEATURE [Part::Box] Box054  label="Nut hole005"
  Height = 6
  Length = 15
  Placement = pos=(-76.5,5,-9.25) rot=(0,-1,0;0.785398rad)
  Width = 3
FEATURE [Part::Box] Box055  label="Nut hole006"
  Height = 6
  Length = 15
  Placement = pos=(23.5,5,-8.25) rot=(0,-1,0;1.5708rad)
  Width = 3
FEATURE [Part::Box] Box056  label="Nut hole007"
  Height = 6
  Length = 15
  Placement = pos=(23.5,5,118.75) rot=(0,-1,0;1.5708rad)
  Width = 3
FEATURE [Part::MultiFuse] Fusion099  label="Nut holes - right dimensions"
  Placement = pos=(0,-3,0) rot=(0,0,1;0rad)
  Shapes = -> [Box056,Box053,Box054,Box052,Box055]
FEATURE [Part::Cut] Cut059  label="Upper tablet holder 002 with nut holes"
  Base = -> Extrude033
  Placement = pos=(-0.5,0,0) rot=(0,0,1;0rad)
  Tool = -> Fusion099
FEATURE [Part::Cylinder] Cylinder032  label="Cylinder017"
  Angle = 360
  Height = 80
  Placement = pos=(41,43,0) rot=(0,0,1;0rad)
  Radius = 25.5
FEATURE [Part::Box] Box057  label="Cube012"
  Height = 90
  Length = 90
  Placement = pos=(0,-12,68) rot=(-1,0,0;0.959931rad)
  Width = 40
FEATURE [Part::Cylinder] Cylinder033  label="Cylinder018"
  Angle = 360
  Height = 80
  Placement = pos=(41,43,0) rot=(0,0,1;0rad)
  Radius = 31.5
FEATURE [Part::Cut] Cut060  label="Tube to tablet piece"
  Base = -> Cylinder033
  Tool = -> Cylinder032
FEATURE [Part::Cut] Cut061
  Base = -> Cut060
  Placement = pos=(0,16,-35) rot=(0,0,1;0rad)
  Tool = -> Box057
FEATURE [Part::Box] Box058  label="Cube013"
  Height = 3
  Length = 80
  Placement = pos=(1,27.5,0) rot=(1,0,0;0.610865rad)
  Width = 80.5
FEATURE [Part::MultiFuse] Fusion101  label="tube to tablet"
  Shapes = -> [Box058,Cut061]
FEATURE [Part::Box] Box059  label="USB hole"
  Height = 13
  Length = 30
  Placement = pos=(3,51,16) rot=(-1,0,0;0.959931rad)
  Width = 13
FEATURE [Part::Cut] Cut062  label="tube to tablet piece"
  Base = -> Fusion101
  Placement = pos=(-37,74,1348) rot=(0,0,1;0rad)
  Tool = -> Box059
FEATURE [Part::Box] Box060  label="Cube014"
  Height = 16
  Length = 16
  Placement = pos=(-83,66,46) rot=(-1,0,0;0.959931rad)
  Width = 16
FEATURE [Part::Box] Box061  label="Cube015"
  Height = 16
  Length = 16
  Placement = pos=(-26,102,72) rot=(-1,0,0;0.959931rad)
  Width = 30
FEATURE [Part::Box] Box062  label="Nut hole008"
  Height = 6
  Length = 15
  Placement = pos=(23.5,5,118.75) rot=(0,-1,0;1.5708rad)
  Width = 4
FEATURE [App::DocumentObjectGroup] Group007  label="Utilities"
  Group = -> [Fusion083,Cylinder022,Fusion091,Box062]
FEATURE [Part::Cut] Cut064  label="US support005"
  Base = -> Fusion059
  Placement = pos=(219,54,0) rot=(0,0,1;1.0472rad)
  Tool = -> Extrude029
FEATURE [Part::Cut] Cut065  label="US support006"
  Base = -> Fusion059
  Placement = pos=(126,0,0) rot=(0,0,1;0rad)
  Tool = -> Extrude029
FEATURE [Part::Mirroring] Part__Mirroring  label="US holes005 (Mirror #3)"
  Base = (5,0,0)
  Normal = (1,0,0)
  Source = -> Fusion057
FEATURE [Part::Mirroring] Part__Mirroring003  label="Bumper walls (Mirror #4)"
  Base = (5,0,0)
  Normal = (1,0,0)
  Source = -> Fusion058
FEATURE [Part::Mirroring] Part__Mirroring004  label="Bumper top with hole (Mirror #5)"
  Base = (5,0,0)
  Normal = (1,0,0)
  Source = -> Cut041
FEATURE [Part::Mirroring] Part__Mirroring005  label="Bumper supports (Mirror #6)"
  Base = (5,0,0)
  Normal = (1,0,0)
  Source = -> Fusion085
FEATURE [Part::MultiFuse] Fusion108  label="US holes006"
  Placement = pos=(-40,0,0) rot=(0,0,1;0rad)
  Shapes = -> [Extrude027,Extrude028]
FEATURE [Part::MultiFuse] Fusion109  label="Bumper walls002"
  Placement = pos=(-40,0,0) rot=(0,0,1;0rad)
  Shapes = -> [Box029,Box030,Cut020]
FEATURE [Part::Cut] Cut066  label="Bumper top with hole001"
  Base = -> Fusion076
  Tool = -> Cylinder021
FEATURE [Part::MultiFuse] Fusion110  label="Bumper supports001"
  Shapes = -> [Cut031,Cut042,Cut032]
FEATURE [Part::MultiFuse] Fusion111  label="Bumper right walls with US supports"
  Shapes = -> [Cut025,Cut024,Fusion109]
FEATURE [Part::Cut] Cut067  label="Bumper wall righ with US supports and holes"
  Base = -> Fusion111
  Tool = -> Fusion108
FEATURE [Part::MultiFuse] Fusion112  label="Bumper right"
  Shapes = -> [Cut067,Cut066,Fusion110]
FEATURE [Part::MultiFuse] Fusion113  label="Bumper left walls with US supports"
  Shapes = -> [Part__Mirroring003,Cut065,Cut064]
FEATURE [Part::Cut] Cut068  label="Bumper walls left with US supports and holes"
  Base = -> Fusion113
  Tool = -> Part__Mirroring
FEATURE [Part::MultiFuse] Fusion114  label="Bumper left"
  Shapes = -> [Cut068,Part__Mirroring005,Part__Mirroring004]
FEATURE [Sketcher::SketchObject] Sketch036  label="battery charger 001"
  Placement = pos=(0,-7,0) rot=(1,0,0;1.5708rad)
  sketch-geometry (10):
    g0: LineSegment StartX=-17.5 StartY=0 StartZ=0 EndX=-17.5 EndY=4 EndZ=0
    g1: LineSegment StartX=-17.5 StartY=4 StartZ=0 EndX=-7.5 EndY=4 EndZ=0
    g2: LineSegment StartX=-7.5 StartY=4 StartZ=0 EndX=-7.5 EndY=6 EndZ=0
    g3: LineSegment StartX=7.5 StartY=6 StartZ=0 EndX=7.5 EndY=4 EndZ=0
    g4: LineSegment StartX=7.5 StartY=4 StartZ=0 EndX=17.5 EndY=4 EndZ=0
    g5: LineSegment StartX=17.5 StartY=4 StartZ=0 EndX=17.5 EndY=0 EndZ=0
    g6: LineSegment StartX=17.5 StartY=0 StartZ=0 EndX=-17.5 EndY=0 EndZ=0
    g7: LineSegment StartX=-7.5 StartY=6 StartZ=0 EndX=-4.75 EndY=6 EndZ=0
    g8: LineSegment StartX=7.5 StartY=6 StartZ=0 EndX=4.75 EndY=6 EndZ=0
    g9: ArcOfCircle CenterX=0 CenterY=6 CenterZ=0 NormalX=0 NormalY=0 NormalZ=1 Radius=4.75 StartAngle=3.14159 EndAngle=6.28319
  constraints (31):
    c: Vertical(g0)
    c: Coincident(g0,g1)
    c: Horizontal(g1)
    c: Coincident(g1,g2)
    c: Vertical(g2)
    c: Vertical(g3)
    c: Coincident(g3,g4)
    c: Horizontal(g4)
    c: Coincident(g4,g5)
    c: Vertical(g5)
    c: Coincident(g5,g6)
    c: Horizontal(g6)
    c: Equal(g0,g5)
    c: Equal(g2,g3)
    c: Equal(g1,g4)
    c: Coincident(g0,g6)
    c: DistanceY(g5,g5) = 4
    c: DistanceX(g4,g4) = 10
    c: DistanceY(g3,g3) = 2
    c: Coincident(g7,g2)
    c: Horizontal(g7)
    c: Horizontal(g8)
    c: Coincident(g9,g7)
    c: Coincident(g9,g8)
    c: Coincident(g3,g8)
    c: Equal(g8,g7)
    c: DistanceX(g8,g8) = 2.75
    c: Radius(g9) = 4.75
    c: DistanceY(g9,g7) = 0
    c: DistanceX(g9,g-1) = 0
    c: DistanceY(g-1,g0) = 0
FEATURE [Sketcher::SketchObject] Sketch037  label="battery charger 002"
  Placement = pos=(0,10,0) rot=(1,0,0;1.5708rad)
  sketch-geometry (10):
    g0: LineSegment StartX=-17.5 StartY=0 StartZ=0 EndX=-17.5 EndY=4 EndZ=0
    g1: LineSegment StartX=-17.5 StartY=4 StartZ=0 EndX=-7.5 EndY=4 EndZ=0
    g2: LineSegment StartX=-7.5 StartY=4 StartZ=0 EndX=-7.5 EndY=6 EndZ=0
    g3: LineSegment StartX=7.5 StartY=6 StartZ=0 EndX=7.5 EndY=4 EndZ=0
    g4: LineSegment StartX=7.5 StartY=4 StartZ=0 EndX=17.5 EndY=4 EndZ=0
    g5: LineSegment StartX=17.5 StartY=4 StartZ=0 EndX=17.5 EndY=0 EndZ=0
    g6: LineSegment StartX=17.5 StartY=0 StartZ=0 EndX=-17.5 EndY=0 EndZ=0
    g7: LineSegment StartX=-7.5 StartY=6 StartZ=0 EndX=-3.5 EndY=6 EndZ=0
    g8: LineSegment StartX=7.5 StartY=6 StartZ=0 EndX=3.5 EndY=6 EndZ=0
    g9: ArcOfCircle CenterX=0 CenterY=6 CenterZ=0 NormalX=0 NormalY=0 NormalZ=1 Radius=3.5 StartAngle=3.14159 EndAngle=6.28319
  constraints (31):
    c: Vertical(g0)
    c: Coincident(g0,g1)
    c: Horizontal(g1)
    c: Coincident(g1,g2)
    c: Vertical(g2)
    c: Vertical(g3)
    c: Coincident(g3,g4)
    c: Horizontal(g4)
    c: Coincident(g4,g5)
    c: Vertical(g5)
    c: Coincident(g5,g6)
    c: Horizontal(g6)
    c: Equal(g0,g5)
    c: Equal(g2,g3)
    c: Equal(g1,g4)
    c: Coincident(g0,g6)
    c: DistanceY(g5,g5) = 4
    c: DistanceX(g4,g4) = 10
    c: DistanceY(g3,g3) = 2
    c: Coincident(g7,g2)
    c: Horizontal(g7)
    c: Horizontal(g8)
    c: Coincident(g9,g7)
    c: Coincident(g9,g8)
    c: Coincident(g3,g8)
    c: Equal(g8,g7)
    c: DistanceX(g8,g8) = 4
    c: Radius(g9) = 3.5
    c: DistanceY(g9,g7) = 0
    c: DistanceX(g-1,g9) = 0
    c: DistanceY(g-1,g0) = 0
FEATURE [Sketcher::SketchObject] Sketch038  label="battery charger 003"
  Placement = pos=(0,0,0) rot=(1,0,0;1.5708rad)
  sketch-geometry (12):
    g0: LineSegment StartX=-17.5 StartY=0 StartZ=0 EndX=-17.5 EndY=4 EndZ=0
    g1: LineSegment StartX=-17.5 StartY=4 StartZ=0 EndX=-7.5 EndY=4 EndZ=0
    g2: LineSegment StartX=-7.5 StartY=4 StartZ=0 EndX=-7.5 EndY=12.5 EndZ=0
    g3: LineSegment StartX=7.5 StartY=12.5 StartZ=0 EndX=7.5 EndY=4 EndZ=0
    g4: LineSegment StartX=7.5 StartY=4 StartZ=0 EndX=17.5 EndY=4 EndZ=0
    g5: LineSegment StartX=17.5 StartY=4 StartZ=0 EndX=17.5 EndY=0 EndZ=0
    g6: LineSegment StartX=7.5 StartY=12.5 StartZ=0 EndX=-7.5 EndY=12.5 EndZ=0
    g7: LineSegment StartX=-17.5 StartY=0 StartZ=0 EndX=-5.5 EndY=0 EndZ=0
    g8: LineSegment StartX=17.5 StartY=0 StartZ=0 EndX=5.5 EndY=0 EndZ=0
    g9: LineSegment StartX=-5.5 StartY=0 StartZ=0 EndX=-5.5 EndY=6 EndZ=0
    g10: LineSegment StartX=5.5 StartY=0 StartZ=0 EndX=5.5 EndY=6 EndZ=0
    g11: ArcOfCircle CenterX=0 CenterY=6 CenterZ=0 NormalX=0 NormalY=0 NormalZ=1 Radius=5.5 StartAngle=0 EndAngle=3.14159
  constraints (37):
    c: Vertical(g0)
    c: Coincident(g0,g1)
    c: Horizontal(g1)
    c: Coincident(g1,g2)
    c: Vertical(g2)
    c: Vertical(g3)
    c: Coincident(g3,g4)
    c: Horizontal(g4)
    c: Coincident(g4,g5)
    c: Vertical(g5)
    c: Equal(g0,g5)
    c: Equal(g2,g3)
    c: Equal(g1,g4)
    c: DistanceY(g5,g5) = 4
    c: DistanceX(g4,g4) = 10
    c: DistanceY(g3,g3) = 8.5
    c: Horizontal(g6)
    c: Coincident(g3,g6)
    c: Coincident(g2,g6)
    c: Coincident(g7,g0)
    c: Horizontal(g7)
    c: Coincident(g8,g5)
    c: Horizontal(g8)
    c: Vertical(g9)
    c: Coincident(g10,g8)
    c: Vertical(g10)
    c: Equal(g9,g10)
    c: Equal(g7,g8)
    c: Coincident(g11,g9)
    c: Coincident(g11,g10)
    c: DistanceY(g9,g11) = 0
    c: DistanceY(g10,g10) = 6
    c: Coincident(g7,g9)
    c: DistanceX(g-1,g11) = 0
    c: DistanceY(g-1,g0) = 0
    c: DistanceX(g6,g6) = 15
    c: Radius(g11) = 5.5
FEATURE [Part::Extrusion] Extrude034  label="Battery charger extruded 001"
  Base = -> Sketch036
  Dir = (0,7,0)
  Solid = true
FEATURE [Part::Extrusion] Extrude035  label="Battery charger extruded 002"
  Base = -> Sketch037
  Dir = (0,10,0)
  Solid = true
FEATURE [Part::Extrusion] Extrude036  label="Battery charger extruded 003"
  Base = -> Sketch038
  Dir = (0,10,0)
  Solid = true
FEATURE [Part::MultiFuse] Fusion115  label="M3 screw001"
  Placement = pos=(14.5,12,5) rot=(0,1,0;3.14159rad)
  Shapes = -> [Cylinder013,Pad003]
FEATURE [Part::MultiFuse] Fusion116  label="M3 screw002"
  Placement = pos=(14.5,2,5) rot=(0,1,0;3.14159rad)
  Shapes = -> [Cylinder013,Pad003]
FEATURE [Part::MultiFuse] Fusion117  label="M3 screw003"
  Placement = pos=(14.5,-6.6,5) rot=(0,1,0;3.14159rad)
  Shapes = -> [Cylinder013,Pad003]
FEATURE [Part::MultiFuse] Fusion118  label="M3 screw004"
  Placement = pos=(-10.5,12,5) rot=(0,1,0;3.14159rad)
  Shapes = -> [Cylinder013,Pad003]
FEATURE [Part::MultiFuse] Fusion119  label="M3 screw005"
  Placement = pos=(-10.5,2,5) rot=(0,1,0;3.14159rad)
  Shapes = -> [Cylinder013,Pad003]
FEATURE [Part::MultiFuse] Fusion120  label="M3 screw006"
  Placement = pos=(-10.5,-6.6,5) rot=(0,1,0;3.14159rad)
  Shapes = -> [Cylinder013,Pad003]
FEATURE [Part::MultiFuse] Fusion121  label="screws 002"
  Shapes = -> [Fusion115,Fusion118]
FEATURE [Part::MultiFuse] Fusion122  label="screws 003"
  Shapes = -> [Fusion116,Fusion119]
FEATURE [Part::MultiFuse] Fusion123  label="screws 001"
  Shapes = -> [Fusion117,Fusion120]
FEATURE [Part::Cut] Cut069  label="Battery charger support 001"
  Base = -> Extrude034
  Placement = pos=(79.7158,259.87,0) rot=(0,0,-1;1.0472rad)
  Tool = -> Fusion123
FEATURE [Part::Cut] Cut070  label="Battery charger support 003"
  Base = -> Extrude036
  Placement = pos=(64.9933,251.37,0) rot=(0,0,-1;1.0472rad)
  Tool = -> Fusion122
FEATURE [Part::Cut] Cut071  label="Battery charger support 002"
  Base = -> Extrude035
  Placement = pos=(47.6728,241.37,0) rot=(0,0,-1;1.0472rad)
  Tool = -> Fusion121
FEATURE [App::DocumentObjectGroup] Group002  label="Electronics / battery"
  Group = -> [Box024,Fusion097,Cut069,Cut070,Cut071]
FEATURE [Part::Cylinder] Cylinder034  label="Battery charger hole"
  Angle = 360
  Height = 20
  Placement = pos=(87.9442,264.725,6) rot=(0.774597,-0.447214,-0.447214;1.82349rad)
  Radius = 4.75
FEATURE [Part::MultiFuse] Fusion124  label="Bumper back holes"
  Shapes = -> [Cylinder034,Fusion045]
FEATURE [Part::Cut] Cut072  label="Bumper back with holes"
  Base = -> Fusion089
  Tool = -> Fusion124
FEATURE [App::DocumentObjectGroup] Group003  label="Bumper"
  Group = -> [User_Library_HC_SR005,Group006,Fusion112,Fusion114,Cut072]
FEATURE [Part::Box] Box063  label="Cube016"
  Height = 37
  Length = 2
  Placement = pos=(201.5,41,3) rot=(0,0,1;0rad)
  Width = 14
FEATURE [Part::Box] Box064  label="Cube017"
  Height = 38
  Length = 8
  Placement = pos=(200.5,41,2) rot=(0,0,1;0rad)
  Width = 14
FEATURE [Part::MultiFuse] Fusion125  label="Encoder support slider"
  Shapes = -> [Box064,Box063,Box048]
FEATURE [Part::Cut] Cut073  label="Encoder support with slider"
  Base = -> Fusion094
  Placement = pos=(-23,15,0) rot=(0,0,1;0rad)
  Tool = -> Fusion125
FEATURE [Part::MultiFuse] Fusion126  label="USB and power buttons001"
  Shapes = -> [Box060,Box061]
FEATURE [Part::MultiFuse] Fusion128  label="Upper tablet holder001"
  Placement = pos=(0,0,0) rot=(-1,0,0;0.959931rad)
  Shapes = -> [Extrude032,Cut059]
FEATURE [Part::Mirroring] Part__Mirroring006  label="Upper tablet holder left"
  Base = (41,53.1823,33.5763)
  Normal = (1,0,-1.19209e-07)
  Placement = pos=(-37.5,69.75,1352.2) rot=(0,0,1;0rad)
  Source = -> Fusion128
FEATURE [Part::Cut] Cut074  label="Upper tablet holder right"
  Base = -> Fusion128
  Placement = pos=(-37,70,1350) rot=(0,0,1;0rad)
  Tool = -> Fusion126
FEATURE [Image::ImagePlane] ImagePlane001
  Placement = pos=(4.5,120.75,1388.2) rot=(1,0,0;0.628319rad)
  XSize = 245
  YSize = 141
FEATURE [Part::Box] Box065  label="Extension tablet 001"
  Height = 4
  Length = 10
  Placement = pos=(-104.491,74.2375,1352.36) rot=(1,0,0;0.610865rad)
  Width = 116
FEATURE [Part::Box] Box066  label="Extension tablet 002"
  Height = 10
  Length = 11
  Placement = pos=(-109.491,86.2375,1350.36) rot=(1,0,0;0.610865rad)
  Width = 15
FEATURE [Part::Box] Box067  label="Extension tablet 003"
  Height = 10
  Length = 11
  Placement = pos=(-109.481,154.029,1398.72) rot=(1,0,0;0.610865rad)
  Width = 15
FEATURE [Part::MultiFuse] Fusion129  label="Upper tablet holder right with fixes"
  Placement = pos=(-0.5,-0.25,2.2) rot=(0,0,1;0rad)
  Shapes = -> [Box065,Box066,Box067,Cut074]
FEATURE [Part::Cylinder] Cylinder035  label="Cylinder019"
  Angle = 360
  Height = 100
  Placement = pos=(24.3,301.8,-30) rot=(0,0,1;0rad)
  Radius = 1.5
FEATURE [Part::Cylinder] Cylinder036  label="Cylinder020"
  Angle = 360
  Height = 100
  Placement = pos=(-18.9,326.8,-30) rot=(0,0,1;0rad)
  Radius = 1.5
FEATURE [Part::Cylinder] Cylinder037  label="Cylinder021"
  Angle = 360
  Height = 100
  Placement = pos=(-46.2,179.8,-30) rot=(0,0,1;0rad)
  Radius = 1.5
FEATURE [Part::Cylinder] Cylinder038  label="Cylinder022"
  Angle = 360
  Height = 100
  Placement = pos=(-89.5,204.8,-30) rot=(0,0,1;0rad)
  Radius = 1.5
FEATURE [Part::Cylinder] Cylinder039  label="Cylinder023"
  Angle = 360
  Height = 100
  Placement = pos=(54.6,259.5,-30) rot=(0,0,1;0rad)
  Radius = 1.5
FEATURE [Part::Cylinder] Cylinder040  label="Cylinder024"
  Angle = 360
  Height = 100
  Placement = pos=(67,237.7,-30) rot=(0,0,1;0rad)
  Radius = 1.5
FEATURE [Part::Cylinder] Cylinder041  label="Cylinder025"
  Angle = 360
  Height = 100
  Placement = pos=(75.8,242.8,-30) rot=(0,0,1;0rad)
  Radius = 1.5
FEATURE [Part::Cylinder] Cylinder042  label="Cylinder026"
  Angle = 360
  Height = 100
  Placement = pos=(82.9,247,-30) rot=(0,0,1;0rad)
  Radius = 1.5
FEATURE [Part::Cylinder] Cylinder043  label="Cylinder027"
  Angle = 360
  Height = 100
  Placement = pos=(63.2,264.5,-30) rot=(0,0,1;0rad)
  Radius = 1.5
FEATURE [Part::Cylinder] Cylinder044  label="Cylinder028"
  Angle = 360
  Height = 100
  Placement = pos=(70.5,268.7,-30) rot=(0,0,1;0rad)
  Radius = 1.5
FEATURE [Part::Cylinder] Cylinder045  label="Cylinder029"
  Angle = 360
  Height = 100
  Placement = pos=(4.5,216,-30) rot=(0,0,1;0rad)
  Radius = 1.5
FEATURE [Part::Cylinder] Cylinder046  label="Cylinder030"
  Angle = 360
  Height = 100
  Placement = pos=(4.5,352,-30) rot=(0,0,1;0rad)
  Radius = 1.5
FEATURE [Part::Cylinder] Cylinder047  label="Cylinder031"
  Angle = 360
  Height = 100
  Placement = pos=(4.5,336.5,-30) rot=(0,0,1;0rad)
  Radius = 1.5
FEATURE [Part::Cylinder] Cylinder048  label="Cylinder032"
  Angle = 360
  Height = 100
  Placement = pos=(126.169,165.578,-20) rot=(0,0,1;0rad)
  Radius = 1.5
FEATURE [Part::Cylinder] Cylinder049  label="Cylinder033"
  Angle = 360
  Height = 100
  Placement = pos=(93.6686,221.87,-20) rot=(0,0,1;0rad)
  Radius = 1.5
FEATURE [Part::Cylinder] Cylinder050  label="Cylinder034"
  Angle = 360
  Height = 100
  Placement = pos=(49.5468,158.291,-20) rot=(0,0,1;0rad)
  Radius = 1.5
FEATURE [Part::Cylinder] Cylinder051  label="Cylinder035"
  Angle = 360
  Height = 100
  Placement = pos=(133.669,152.588,-20) rot=(0,0,1;0rad)
  Radius = 1.5
FEATURE [Part::Cylinder] Cylinder052  label="Cylinder036"
  Angle = 360
  Height = 100
  Placement = pos=(126.5,22.75,-40) rot=(0,0,1;0rad)
  Radius = 1.5
FEATURE [Part::Cylinder] Cylinder053  label="Cylinder037"
  Angle = 360
  Height = 100
  Placement = pos=(155.5,12,-20) rot=(0,0,1;0rad)
  Radius = 1.5
FEATURE [Part::Cylinder] Cylinder054  label="Cylinder038"
  Angle = 360
  Height = 100
  Placement = pos=(4.5,82,-20) rot=(0,0,1;0rad)
  Radius = 1.5
FEATURE [Part::Cylinder] Cylinder055  label="Cylinder039"
  Angle = 360
  Height = 100
  Placement = pos=(37.5,12,-20) rot=(0,0,1;0rad)
  Radius = 1.5
FEATURE [Part::Cylinder] Cylinder056  label="Cylinder040"
  Angle = 360
  Height = 100
  Placement = pos=(-27.5,12,-20) rot=(0,0,1;0rad)
  Radius = 1.5
FEATURE [Part::Cylinder] Cylinder057  label="Cylinder041"
  Angle = 360
  Height = 100
  Placement = pos=(-97.5,125.25,-40) rot=(0,0,1;0rad)
  Radius = 1.5
FEATURE [Part::Cylinder] Cylinder058  label="Cylinder042"
  Angle = 360
  Height = 100
  Placement = pos=(-46.914,143.734,-20) rot=(0,0,1;0rad)
  Radius = 1.5
FEATURE [Part::Cylinder] Cylinder059  label="Cylinder043"
  Angle = 360
  Height = 100
  Placement = pos=(-115.303,165.078,-20) rot=(0,0,1;0rad)
  Radius = 1.5
FEATURE [Part::Cylinder] Cylinder060  label="Cylinder044"
  Angle = 360
  Height = 100
  Placement = pos=(86.2,234.8,-50) rot=(0,0,1;0rad)
  Radius = 1.5
FEATURE [Part::Cylinder] Cylinder061  label="Cylinder045"
  Angle = 360
  Height = 100
  Placement = pos=(-123.669,152.588,-20) rot=(0,0,1;0rad)
  Radius = 1.5
FEATURE [Part::Cylinder] Cylinder062  label="Cylinder046"
  Angle = 360
  Height = 100
  Placement = pos=(-145.5,12,-20) rot=(0,0,1;0rad)
  Radius = 1.5
FEATURE [Part::Cylinder] Cylinder063  label="Cylinder047"
  Angle = 360
  Height = 100
  Placement = pos=(110.5,22.75,-40) rot=(0,0,1;0rad)
  Radius = 1.5
FEATURE [Part::Cylinder] Cylinder064  label="Cylinder048"
  Angle = 360
  Height = 100
  Placement = pos=(107.5,125.25,-40) rot=(0,0,1;0rad)
  Radius = 1.5
FEATURE [Part::Cylinder] Cylinder065  label="Cylinder049"
  Angle = 360
  Height = 100
  Placement = pos=(129.5,125.25,-40) rot=(0,0,1;0rad)
  Radius = 1.5
FEATURE [Part::Cylinder] Cylinder066  label="Cylinder050"
  Angle = 360
  Height = 100
  Placement = pos=(30.6275,158.852,-40) rot=(0,0,1;0rad)
  Radius = 1.5
FEATURE [Part::Cylinder] Cylinder067  label="Cylinder051"
  Angle = 360
  Height = 100
  Placement = pos=(30.6275,107.552,-40) rot=(0,0,1;0rad)
  Radius = 1.5
FEATURE [Part::Cylinder] Cylinder068  label="Cylinder052"
  Angle = 360
  Height = 100
  Placement = pos=(-20.6725,107.552,-40) rot=(0,0,1;0rad)
  Radius = 1.5
FEATURE [Part::Cylinder] Cylinder069  label="Cylinder053"
  Angle = 360
  Height = 100
  Placement = pos=(-20.6725,158.852,-40) rot=(0,0,1;0rad)
  Radius = 1.5
FEATURE [Part::Cylinder] Cylinder070  label="Cylinder054"
  Angle = 360
  Height = 100
  Placement = pos=(72.5,94,-20) rot=(0,0,1;0rad)
  Radius = 1.5
FEATURE [Part::Mirroring] Part__Mirroring007  label="Wheel (Mirror #7)"
  Base = (5,0,0)
  Normal = (1,0,0)
  Source = -> Cylinder
FEATURE [Part::Mirroring] Part__Mirroring009  label="Encoder-to-wheel piece (Mirror #9)"
  Base = (5,0,0)
  Normal = (1,0,0)
  Source = -> Cut055
FEATURE [Part::Cylinder] Cylinder071  label="Cylinder055"
  Angle = 360
  Height = 100
  Placement = pos=(-119.5,125.25,-40) rot=(0,0,1;0rad)
  Radius = 1.5
FEATURE [Part::Cylinder] Cylinder072  label="Cylinder056"
  Angle = 360
  Height = 100
  Placement = pos=(-116.5,22.75,-40) rot=(0,0,1;0rad)
  Radius = 1.5
FEATURE [Part::Cylinder] Cylinder073  label="Cylinder057"
  Angle = 360
  Height = 100
  Placement = pos=(-100.5,22.75,-40) rot=(0,0,1;0rad)
  Radius = 1.5
FEATURE [Part::Cylinder] Cylinder074  label="Cylinder058"
  Angle = 360
  Height = 100
  Placement = pos=(-62.5,94,-20) rot=(0,0,1;0rad)
  Radius = 1.5
FEATURE [Part::Box] Box068  label="Cube018"
  Height = 100
  Length = 30
  Placement = pos=(133,23,-40) rot=(0,0,1;0rad)
  Width = 80
FEATURE [Part::Mirroring] Part__Mirroring011  label="Wheel base holes"
  Base = (5,0,0)
  Normal = (1,0,0)
  Source = -> Box068
FEATURE [Part::MultiFuse] Fusion130  label="Base holes"
  Shapes = -> [Box068,Part__Mirroring011,Cylinder069,Cylinder068,Cylinder070,Cylinder072,Cylinder073,Cylinder074,Cylinder054,Cylinder055,Cylinder056,Cylinder057,Cylinder058,Cylinder059,Cylinder061,Cylinder062,Cylinder060,Cylinder064,Cylinder065,Cylinder066,Cylinder035,Cylinder041,Cylinder037,Cylinder038,Cylinder039,Cylinder036,Cylinder048,Cylinder042,Cylinder047,Cylinder044,Cylinder049,Cylinder045,Cylinder051,+9 more]
FEATURE [Part::Cut] Cut075  label="Base with holes"
  Base = -> Extrude012
  Tool = -> Fusion130
FEATURE [Part::Part2DObjectPython] Shape2DView  label="DXF base with holes"  # Draft 2D object (typed FeaturePython)
  Base = -> Cut075
  HiddenLines = false
  Projection = (0,0,-1)
  ProjectionMode = 0
  SegmentLength = 0.05
  Tessellation = false
FEATURE [App::DocumentObjectGroup] Group004  label="Base and cuts"
  Group = -> [Point,Cut075,Shape2DView]
FEATURE [Part::Box] Box069  label="Cables cut encoder piece"
  Height = 15
  Length = 8
  Placement = pos=(170.769,55,44.0053) rot=(0,0,1;0rad)
  Width = 15
FEATURE [Part::Cut] Cut076  label="Encoder support with slider and cables hole"
  Base = -> Cut073
  Tool = -> Box069
FEATURE [Sketcher::SketchObject] Sketch039
  sketch-geometry (4):
    g0: LineSegment StartX=-2.99986 StartY=1.51885 StartZ=0 EndX=-2.99986 EndY=11.5188 EndZ=0
    g1: LineSegment StartX=-2.99986 StartY=11.5188 StartZ=0 EndX=12.0001 EndY=11.5188 EndZ=0
    g2: LineSegment StartX=12.0001 StartY=11.5188 StartZ=0 EndX=12.0001 EndY=1.51885 EndZ=0
    g3: LineSegment StartX=12.0001 StartY=1.51885 StartZ=0 EndX=-2.99986 EndY=1.51885 EndZ=0
  constraints (10):
    c: Coincident(g0,g1)
    c: Horizontal(g1)
    c: Coincident(g1,g2)
    c: Coincident(g2,g3)
    c: Coincident(g3,g0)
    c: Horizontal(g3)
    c: DistanceX(g1,g1) = 15
    c: DistanceX(g3,g3) = 15
    c: DistanceY(g2,g1) = 10
    c: DistanceX(g2,g1) = 0
FEATURE [Part::Extrusion] Extrude037  label="Tab"
  Base = -> Sketch039
  Dir = (0,0,5)
  Placement = pos=(142.992,57.6812,49.0053) rot=(0,0,1;1.5708rad)
  Solid = true
FEATURE [Part::MultiFuse] Fusion131  label="Motor holder with tab"
  Shapes = -> [Extrude037,Cut006]
FEATURE [Sketcher::SketchObject] Sketch040
  sketch-geometry (4):
    g0: LineSegment StartX=-4.55141 StartY=1.36738 StartZ=0 EndX=-4.55141 EndY=10.3674 EndZ=0
    g1: LineSegment StartX=-4.55141 StartY=10.3674 StartZ=0 EndX=10.9486 EndY=10.3674 EndZ=0
    g2: LineSegment StartX=10.9486 StartY=10.3674 StartZ=0 EndX=10.9486 EndY=1.36738 EndZ=0
    g3: LineSegment StartX=10.9486 StartY=1.36738 StartZ=0 EndX=-4.55141 EndY=1.36738 EndZ=0
  constraints (10):
    c: Coincident(g0,g1)
    c: Horizontal(g1)
    c: Coincident(g1,g2)
    c: Coincident(g2,g3)
    c: Coincident(g3,g0)
    c: Horizontal(g3)
    c: DistanceX(g1,g1) = 15.5
    c: DistanceX(g3,g3) = 15.5
    c: DistanceY(g2,g1) = 9
    c: DistanceX(g2,g1) = 0
FEATURE [Part::Extrusion] Extrude038  label="Tab001"
  Base = -> Sketch040
  Dir = (0,0,6)
  Placement = pos=(142.792,58.9812,48.0053) rot=(0,0,1;1.5708rad)
  Solid = true
FEATURE [Part::Cut] Cut077  label="Encoder support with tab"
  Base = -> Cut076
  Tool = -> Extrude038
FEATURE [Part::Mirroring] Part__Mirroring012  label="Motor holder with tab (Mirror #10)"
  Base = (5,0,0)
  Normal = (1,0,0)
  Source = -> Fusion131
FEATURE [Part::Box] Box070  label="Cube019"
  Height = 5
  Length = 52
  Placement = pos=(154.769,38,49.0053) rot=(0,0,1;0rad)
  Width = 23
FEATURE [Part::Box] Box071  label="Cube020"
  Height = 49
  Length = 5
  Placement = pos=(201.769,38,0.00526065) rot=(0,0,1;0rad)
  Width = 23
FEATURE [Part::MultiFuse] Fusion132  label="Encoder support001"
  Placement = pos=(0,-4,0) rot=(0,0,1;0rad)
  Shapes = -> [Box070,Box071]
FEATURE [Part::Box] Box072  label="Cube021"
  Height = 40
  Length = 2
  Placement = pos=(203.5,37,2) rot=(0,0,1;0rad)
  Width = 19
FEATURE [Part::Box] Box073  label="Cube022"
  Height = 37
  Length = 2
  Placement = pos=(201.5,38,3) rot=(0,0,1;0rad)
  Width = 14
FEATURE [Part::Box] Box074  label="Cube023"
  Height = 38
  Length = 8
  Placement = pos=(200.5,38,2) rot=(0,0,1;0rad)
  Width = 14
FEATURE [Part::MultiFuse] Fusion133  label="Encoder support slider001"
  Placement = pos=(0,-2,0) rot=(0,0,1;0rad)
  Shapes = -> [Box074,Box073,Box072]
FEATURE [Part::Cut] Cut078  label="Encoder support with slider001"
  Base = -> Fusion132
  Placement = pos=(-23,15,0) rot=(0,0,1;0rad)
  Tool = -> Fusion133
FEATURE [Part::Box] Box075  label="Cables cut encoder piece001"
  Height = 15
  Length = 8
  Placement = pos=(170.769,55,44.0053) rot=(0,0,1;0rad)
  Width = 15
FEATURE [Part::Cut] Cut079  label="Encoder support with slider and cables hole001"
  Base = -> Cut078
  Tool = -> Box075
FEATURE [Sketcher::SketchObject] Sketch041
  sketch-geometry (4):
    g0: LineSegment StartX=-4.55141 StartY=1.36738 StartZ=0 EndX=-4.55141 EndY=10.3674 EndZ=0
    g1: LineSegment StartX=-4.55141 StartY=10.3674 StartZ=0 EndX=10.9486 EndY=10.3674 EndZ=0
    g2: LineSegment StartX=10.9486 StartY=10.3674 StartZ=0 EndX=10.9486 EndY=1.36738 EndZ=0
    g3: LineSegment StartX=10.9486 StartY=1.36738 StartZ=0 EndX=-4.55141 EndY=1.36738 EndZ=0
  constraints (10):
    c: Coincident(g0,g1)
    c: Horizontal(g1)
    c: Coincident(g1,g2)
    c: Coincident(g2,g3)
    c: Coincident(g3,g0)
    c: Horizontal(g3)
    c: DistanceX(g1,g1) = 15.5
    c: DistanceX(g3,g3) = 15.5
    c: DistanceY(g2,g1) = 9
    c: DistanceX(g2,g1) = 0
FEATURE [Part::Extrusion] Extrude039  label="Tab002"
  Base = -> Sketch041
  Dir = (0,0,6)
  Placement = pos=(142.792,58.9812,48.0053) rot=(0,0,1;1.5708rad)
  Solid = true
FEATURE [Part::Cut] Cut080  label="Encoder support with tab001"
  Base = -> Cut079
  Tool = -> Extrude039
FEATURE [Part::Mirroring] Part__Mirroring013  label="Encoder support with tab001 (Mirror #11)"
  Base = (5,0,0)
  Normal = (1,0,0)
  Source = -> Cut080
FEATURE [App::DocumentObjectGroup] Group001  label="Wheels"
  Group = -> [Box006,Cylinder,Cut055,Part__Mirroring007,Part__Mirroring009,Part__Mirroring012,Cut077,Part__Mirroring013]
FEATURE [Part::Box] Box076  label="base"
  Height = 5
  Length = 60
  Placement = pos=(-25,103,0) rot=(0,0,1;0rad)
  Width = 60
FEATURE [Part::Cylinder] Cylinder075  label="Cylinder084"
  Angle = 360
  Height = 100
  Placement = pos=(30.6275,158.852,-40) rot=(0,0,1;0rad)
  Radius = 1.5
FEATURE [Part::Cylinder] Cylinder076  label="Cylinder085"
  Angle = 360
  Height = 100
  Placement = pos=(-20.6725,158.852,-40) rot=(0,0,1;0rad)
  Radius = 1.5
FEATURE [Part::Cylinder] Cylinder077  label="Cylinder086"
  Angle = 360
  Height = 100
  Placement = pos=(-20.6725,107.552,-40) rot=(0,0,1;0rad)
  Radius = 1.5
FEATURE [Part::Cylinder] Cylinder078  label="Cylinder087"
  Angle = 360
  Height = 100
  Placement = pos=(30.6275,107.552,-40) rot=(0,0,1;0rad)
  Radius = 1.5
FEATURE [Part::MultiFuse] Fusion134  label="base-screwholes"
  Shapes = -> [Cylinder075,Cylinder078,Cylinder077,Cylinder076]
FEATURE [Part::Cone] Cone
  Angle = 360
  Height = 40
  Placement = pos=(5,133,5) rot=(0,0,1;0rad)
  Radius1 = 42.3
  Radius2 = 28
FEATURE [Part::Cylinder] Cylinder079  label="tube-outer"
  Angle = 360
  Height = 50
  Placement = pos=(5,133,5) rot=(0,0,1;0rad)
  Radius = 25.5
FEATURE [Part::Cut] Cut081
  Base = -> Cone
  Tool = -> Cylinder079
FEATURE [Part::Cylinder] Cylinder080  label="tube-inner"
  Angle = 360
  Height = 50
  Placement = pos=(5,133,5) rot=(0,0,1;0rad)
  Radius = 20.75
FEATURE [Part::Box] Box077  label="Cube025"
  Height = 50
  Length = 100
  Placement = pos=(-45,83,0) rot=(0,0,1;0rad)
  Width = 100
FEATURE [Part::Box] Box078  label="Cube026"
  Height = 50
  Length = 60
  Placement = pos=(-25,103,0) rot=(0,0,1;0rad)
  Width = 60
FEATURE [Part::Cut] Cut082  label="outer-square-frame"
  Base = -> Box077
  Tool = -> Box078
FEATURE [Part::Cut] Cut083  label="tube-holder"
  Base = -> Cut081
  Tool = -> Cut082
FEATURE [Part::MultiFuse] Fusion135
  Shapes = -> [Box076,Cylinder080,Cut083]
FEATURE [Part::Cut] Cut084
  Base = -> Fusion135
  Tool = -> Fusion134
FEATURE [Part::MultiFuse] Fusion136  label="M3 screw007"
  Placement = pos=(32.35,104.6,21) rot=(0,1,0;3.14159rad)
  Shapes = -> [Cylinder013,Pad003]
FEATURE [Part::FeaturePython] Array  # Draft array (typed FeaturePython)
  Angle = 360
  ArrayType = 0
  Axis = (0,0,1)
  Base = -> Fusion136
  Center = (0,0,0)
  Fuse = false
  IntervalAxis = (0,0,0)
  IntervalX = (-51.25,0,0)
  IntervalY = (0,51.25,0)
  IntervalZ = (0,0,0)
  NumberPolar = 1
  NumberX = 2
  NumberY = 2
  NumberZ = 1
FEATURE [Part::Cut] Cut085  label="shaftHolder"
  Base = -> Cut084
  Tool = -> Array
FEATURE [Part::Cylinder] Cylinder082  label="Cylinder088"
  Angle = 360
  Height = 1350
  Placement = pos=(5,133,5.55) rot=(0,0,1;0rad)
  Radius = 26
FEATURE [Part::MultiFuse] Fusion137  label="Rear tablet holder001"
  Placement = pos=(-37.5,69.75,1352.2) rot=(0,0,1;0rad)
  Shapes = -> [Part__Mirroring001,Extrude031]
FEATURE [Part::Box] Box079  label="Cube027"
  Height = 5
  Length = 81
  Placement = pos=(0.5,22,0) rot=(0,0,1;0rad)
  Width = 81.68
FEATURE [Part::Box] Box080  label="Cube028"
  Height = 5
  Length = 51
  Placement = pos=(15.5,-9.9875,0) rot=(0,0,1;0rad)
  Width = 145.7
FEATURE [Part::MultiFuse] Fusion138
  Shapes = -> [Box079,Box080]
FEATURE [Part::Cylinder] Cylinder083  label="Cylinder089"
  Angle = 360
  Height = 10
  Placement = pos=(20.55,-5,0) rot=(0,0,1;0rad)
  Radius = 2
FEATURE [Part::FeaturePython] Array001  # Draft array (typed FeaturePython)
  Angle = 360
  ArrayType = 0
  Axis = (0,0,1)
  Base = -> Cylinder083
  Center = (0,0,0)
  Fuse = false
  IntervalAxis = (0,0,0)
  IntervalX = (40.9,0,0)
  IntervalY = (0,135.7,0)
  IntervalZ = (0,0,0)
  NumberPolar = 1
  NumberX = 2
  NumberY = 2
  NumberZ = 1
  Placement = pos=(0,0,-2) rot=(0,0,1;0rad)
FEATURE [Part::Cut] Cut086  label="tablet-holder-plate"
  Base = -> Fusion138
  Placement = pos=(-37.5,80.75,1337.2) rot=(1,0,0;0.610865rad)
  Tool = -> Array001
FEATURE [App::DocumentObjectGroup] Group008  label="Tubes and tablet"
  Group = -> [Cut058,Cut062,Box051,Part__Mirroring006,ImagePlane001,Fusion129,Cylinder082,Cut085,Fusion137,Cut086]
